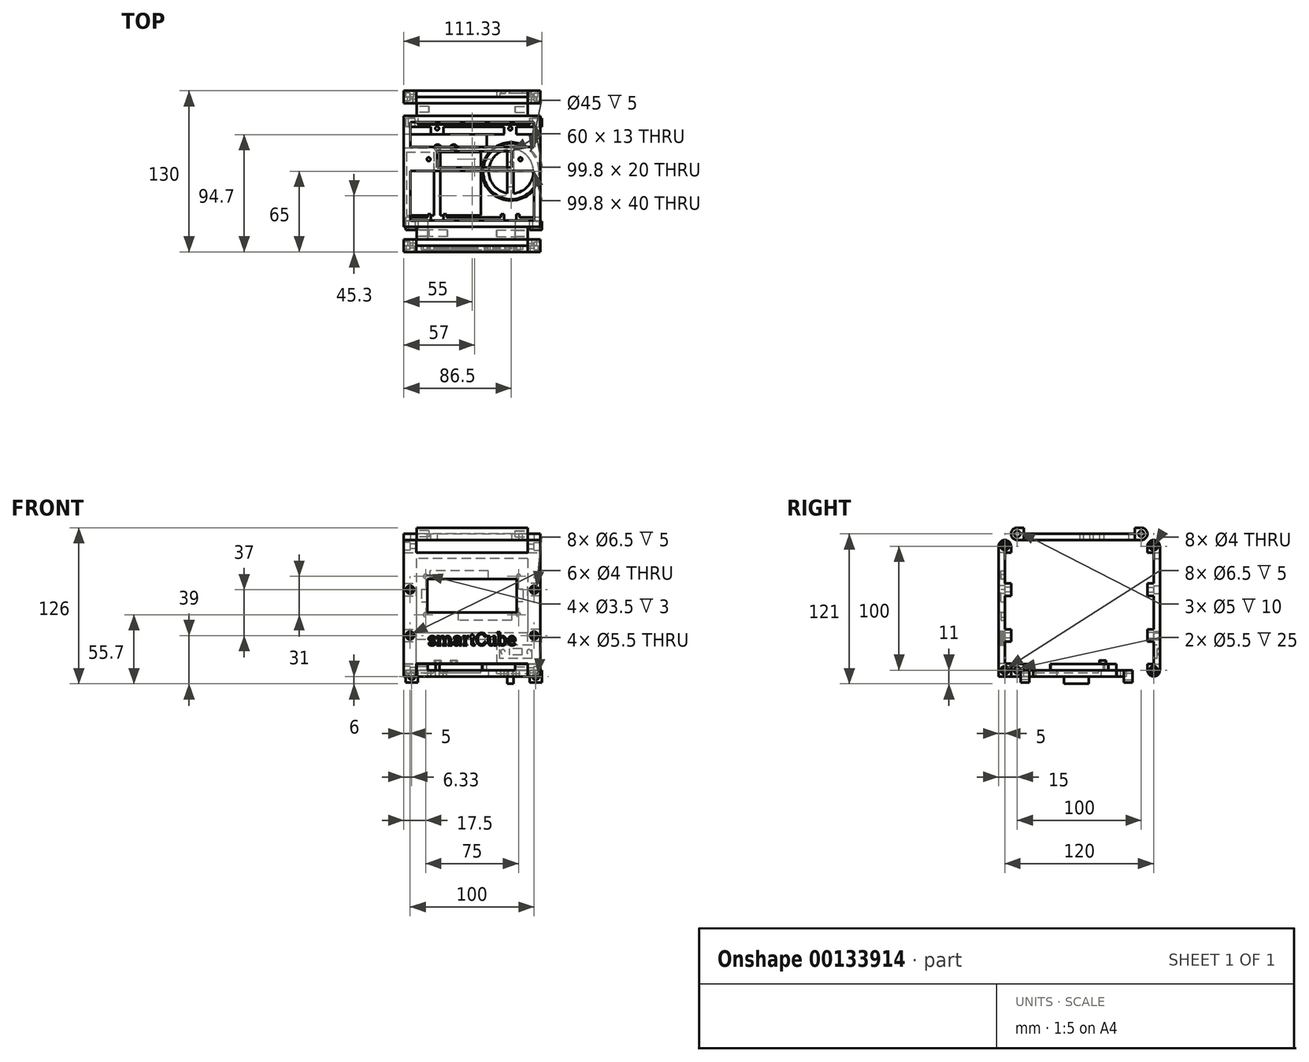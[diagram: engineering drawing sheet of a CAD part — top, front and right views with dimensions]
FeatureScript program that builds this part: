
annotation { "Feature Type Name" : "Feature", "Feature Type Description" : "" }
export const myFeature = defineFeature(function(context is Context, id is Id, definition is map)
    precondition{}
    {
        {
            assignVariable(context, id + "F0", {"name" : "wallthickness", "anyValue" : 10});
        }
        {
            var Q0;
            Q0=qCreatedBy(makeId("Top.planeOp"),FACE);
            var sketch = newSketch(context, id + "F1", { "sketchPlane" : qUnion([Q0])});
            skLineSegment(sketch, "E0.bottom", {"start": v(55, 55) * mm, "end": v(-55, 55) * mm});
            skLineSegment(sketch, "E0.top", {"start": v(55, -55) * mm, "end": v(-55, -55) * mm});
            skLineSegment(sketch, "E0.left", {"start": v(55, 55) * mm, "end": v(55, -55) * mm});
            skLineSegment(sketch, "E0.right", {"start": v(-55, 55) * mm, "end": v(-55, -55) * mm});
            skPoint(sketch, "E0.middle", {"position": v(0, 0) * mm});
            skSolve(sketch);
        }
        {
            var Q0;
            Q0 = qSketchRegion(id + "F1", true);
            var Q1;
            Q1=makeQuery(id+"F1.imprint","IMPRINT",FACE,{"disambiguationData":[TD([[makeQuery(id+"F1.imprint","IMPRINT",EDGE,{"derivedFrom":sQuery(id+"F1.wireOp",EDGE,"Ik4GJv2W-OQxF-1Uup-oVkI-S9FSixUqUyaa.bottom")}),1.0]])]});
            var Q2;
            Q2=makeQuery(id+"F1.imprint","IMPRINT",FACE,{"disambiguationData":[TD([[makeQuery(id+"F1.imprint","IMPRINT",EDGE,{"derivedFrom":sQuery(id+"F1.wireOp",EDGE,"4651642c-b40e-41a3-8e81-cadb49717aff")}),-1.0]])]});
            var Q3;
            Q3=makeQuery(id+"F1.imprint","IMPRINT",FACE,{"disambiguationData":[TD([[makeQuery(id+"F1.imprint","IMPRINT",EDGE,{"derivedFrom":sQuery(id+"F1.wireOp",EDGE,"6e1fa858-a5c8-444f-bbba-da70f5c4369a")}),-1.0]])]});
            var Q4;
            Q4=makeQuery(id+"F1.imprint","IMPRINT",FACE,{"disambiguationData":[TD([[makeQuery(id+"F1.imprint","IMPRINT",EDGE,{"derivedFrom":sQuery(id+"F1.wireOp",EDGE,"c5d3db0a-0530-42fc-989c-932ff3de016f")}),-1.0]])]});
            var Q5;
            Q5=makeQuery(id+"F1.imprint","IMPRINT",FACE,{"disambiguationData":[TD([[makeQuery(id+"F1.imprint","IMPRINT",EDGE,{"derivedFrom":sQuery(id+"F1.wireOp",EDGE,"a261eff7-1251-44c3-8bcb-5ba957302f77")}),-1.0]])]});
            extrude(context, id + "F2", {"entities" : qUnion([Q0, Q1, Q2, Q3, Q4, Q5]), "depth" : (getVariable(context, 'wallthickness')) * mm});
        }
        {
            var Q0;
            Q0=makeQuery(id+"F2.opExtrude","CAP_FACE",FACE,{"disambiguationData":[OSD([sQuery(id+"F1.wireOp",EDGE,"E0.bottom"),sQuery(id+"F1.wireOp",EDGE,"E0.top"),sQuery(id+"F1.wireOp",EDGE,"E0.left"),sQuery(id+"F1.wireOp",EDGE,"E0.right")])],"isStart":false});
            var sketch = newSketch(context, id + "F3", { "sketchPlane" : qUnion([Q0])});
            skLineSegment(sketch, "E1.bottom", {"start": v(55, 55) * mm, "end": v(44.8, 55) * mm});
            skLineSegment(sketch, "E1.top", {"start": v(55, 44.8) * mm, "end": v(44.8, 44.8) * mm});
            skLineSegment(sketch, "E1.left", {"start": v(55, 55) * mm, "end": v(55, 44.8) * mm});
            skLineSegment(sketch, "E1.right", {"start": v(44.8, 55) * mm, "end": v(44.8, 44.8) * mm});
            skLineSegment(sketch, "E2.bottom", {"start": v(-55, 55) * mm, "end": v(-44.8, 55) * mm});
            skLineSegment(sketch, "E2.top", {"start": v(-55, 44.8) * mm, "end": v(-44.8, 44.8) * mm});
            skLineSegment(sketch, "E2.left", {"start": v(-55, 55) * mm, "end": v(-55, 44.8) * mm});
            skLineSegment(sketch, "E2.right", {"start": v(-44.8, 55) * mm, "end": v(-44.8, 44.8) * mm});
            skLineSegment(sketch, "E3.bottom", {"start": v(-55, -55) * mm, "end": v(-44.8, -55) * mm});
            skLineSegment(sketch, "E3.top", {"start": v(-55, -44.8) * mm, "end": v(-44.8, -44.8) * mm});
            skLineSegment(sketch, "E3.left", {"start": v(-55, -55) * mm, "end": v(-55, -44.8) * mm});
            skLineSegment(sketch, "E3.right", {"start": v(-44.8, -55) * mm, "end": v(-44.8, -44.8) * mm});
            skLineSegment(sketch, "E4.bottom", {"start": v(55, -55) * mm, "end": v(44.8, -55) * mm});
            skLineSegment(sketch, "E4.top", {"start": v(55, -44.8) * mm, "end": v(44.8, -44.8) * mm});
            skLineSegment(sketch, "E4.left", {"start": v(55, -55) * mm, "end": v(55, -44.8) * mm});
            skLineSegment(sketch, "E4.right", {"start": v(44.8, -55) * mm, "end": v(44.8, -44.8) * mm});
            skSolve(sketch);
        }
        {
            var Q0;
            Q0 = qSketchRegion(id + "F3", true);
            extrude(context, id + "F4", {"entities" : qUnion([Q0]), "operationType" : NewBodyOperationType.REMOVE, "oppositeDirection" : true, "depth" : (getVariable(context, 'wallthickness')) * mm});
        }
        {
            var Q0;
            Q0=makeQuery(id+"F4.boolean.opBoolean","COPY",FACE,{"derivedFrom":makeQuery(id+"F4.opExtrude","SWEPT_FACE",FACE,{"disambiguationData":[OSD([sQuery(id+"F3.wireOp",EDGE,"E3.right")])]})});
            var sketch = newSketch(context, id + "F5", { "sketchPlane" : qUnion([Q0])});
            skCircle(sketch, "E5", {"center": v(50, 5) * mm, "radius": 2.75 * mm});
            skSolve(sketch);
        }
        {
            var Q0;
            Q0 = qSketchRegion(id + "F5", true);
            extrude(context, id + "F6", {"entities" : qUnion([Q0]), "operationType" : NewBodyOperationType.REMOVE, "oppositeDirection" : true, "depth" : 25 * mm});
        }
        {
            var Q0;
            Q0=makeQuery(id+"F4.boolean.opBoolean","COPY",FACE,{"derivedFrom":makeQuery(id+"F4.opExtrude","SWEPT_FACE",FACE,{"disambiguationData":[OSD([sQuery(id+"F3.wireOp",EDGE,"E4.right")])]})});
            var sketch = newSketch(context, id + "F7", { "sketchPlane" : qUnion([Q0])});
            skCircle(sketch, "E6", {"center": v(-50, 5) * mm, "radius": 2.75 * mm});
            skSolve(sketch);
        }
        {
            var Q0;
            Q0 = qSketchRegion(id + "F7", true);
            extrude(context, id + "F8", {"entities" : qUnion([Q0]), "operationType" : NewBodyOperationType.REMOVE, "oppositeDirection" : true, "depth" : 25 * mm});
        }
        {
            var Q0;
            Q0=makeQuery(id+"F4.boolean.opBoolean","COPY",FACE,{"derivedFrom":makeQuery(id+"F4.opExtrude","SWEPT_FACE",FACE,{"disambiguationData":[OSD([sQuery(id+"F3.wireOp",EDGE,"E2.right")])]})});
            var sketch = newSketch(context, id + "F9", { "sketchPlane" : qUnion([Q0])});
            skCircle(sketch, "E7", {"center": v(-50, 5) * mm, "radius": 2.75 * mm});
            skSolve(sketch);
        }
        {
            var Q0;
            Q0 = qSketchRegion(id + "F9", true);
            extrude(context, id + "F10", {"entities" : qUnion([Q0]), "operationType" : NewBodyOperationType.REMOVE, "oppositeDirection" : true, "depth" : 25 * mm});
        }
        {
            var Q0;
            Q0=makeQuery(id+"F4.boolean.opBoolean","COPY",FACE,{"derivedFrom":makeQuery(id+"F4.opExtrude","SWEPT_FACE",FACE,{"disambiguationData":[OSD([sQuery(id+"F3.wireOp",EDGE,"E1.right")])]})});
            var sketch = newSketch(context, id + "F11", { "sketchPlane" : qUnion([Q0])});
            skCircle(sketch, "E8", {"center": v(50, 5) * mm, "radius": 2.75 * mm});
            skSolve(sketch);
        }
        {
            var Q0;
            Q0 = qSketchRegion(id + "F11", true);
            extrude(context, id + "F12", {"entities" : qUnion([Q0]), "operationType" : NewBodyOperationType.REMOVE, "oppositeDirection" : true, "depth" : 25 * mm});
        }
        {
            var Q0;
            Q0=makeQuery(id+"F2.opExtrude","SWEPT_FACE",FACE,{"disambiguationData":[OSD([sQuery(id+"F1.wireOp",EDGE,"E0.top")])]});
            var sketch = newSketch(context, id + "F13", { "sketchPlane" : qUnion([Q0])});
            skLineSegment(sketch, "E9.0", {"start": v(55, 0) * mm, "end": v(-55, 0) * mm});
            skLineSegment(sketch, "E10.bottom", {"start": v(-55, 0) * mm, "end": v(55, 0) * mm});
            skLineSegment(sketch, "E10.top", {"start": v(-55, 110) * mm, "end": v(55, 110) * mm});
            skLineSegment(sketch, "E10.left", {"start": v(-55, 0) * mm, "end": v(-55, 110) * mm});
            skLineSegment(sketch, "E10.right", {"start": v(55, 0) * mm, "end": v(55, 110) * mm});
            skSolve(sketch);
        }
        {
            var Q0;
            Q0=makeQuery(id+"F13.imprint","IMPRINT",FACE,{"disambiguationData":[TD([[makeQuery(id+"F13.imprint","IMPRINT",EDGE,{"derivedFrom":sQuery(id+"F13.wireOp",EDGE,"E10.top")}),-1.0]])]});
            var Q1;
            {var subQ1=sQuery(id+"F1.wireOp",EDGE,"E0.top");Q1=makeQuery(id+"F13.imprint","IMPRINT",FACE,{"disambiguationData":[TD([[makeQuery(id+"F13.imprint","IMPRINT",EDGE,{"derivedFrom":makeQuery(id+"FIyDD7IV5j6uFW4_2.opFillet","BLEND_EDGE",EDGE,{"blendedFrom":[makeQuery(id+"F2.opExtrude","CAP_EDGE",EDGE,{"disambiguationData":[OSD([subQ1])],"isStart":false}),makeQuery(id+"F2.opExtrude","SWEPT_FACE",FACE,{"disambiguationData":[OSD([subQ1])]})],"blendedInto":[makeQuery(id+"F2.opExtrude","SWEPT_FACE",FACE,{"disambiguationData":[OSD([subQ1])]})]})}),1.0]])]});}
            extrude(context, id + "F14", {"entities" : qUnion([Q0, Q1]), "depth" : (getVariable(context, 'wallthickness')) * mm});
        }
        {
            var Q0;
            Q0=makeQuery(id+"F14.opExtrude","CAP_FACE",FACE,{"disambiguationData":[OSD([sQuery(id+"F13.wireOp",EDGE,"E10.bottom"),sQuery(id+"F13.wireOp",EDGE,"E10.top"),sQuery(id+"F13.wireOp",EDGE,"E10.left"),sQuery(id+"F13.wireOp",EDGE,"E10.right")])],"isStart":false});
            var sketch = newSketch(context, id + "F15", { "sketchPlane" : qUnion([Q0])});
            skLineSegment(sketch, "E11.bottom", {"start": v(-55, 0) * mm, "end": v(-45, 0) * mm});
            skLineSegment(sketch, "E11.top", {"start": v(-55, 10.2) * mm, "end": v(-45, 10.2) * mm});
            skLineSegment(sketch, "E11.left", {"start": v(-55, 0) * mm, "end": v(-55, 10.2) * mm});
            skLineSegment(sketch, "E11.right", {"start": v(-45, 0) * mm, "end": v(-45, 10.2) * mm});
            skLineSegment(sketch, "E12.bottom", {"start": v(55, 0) * mm, "end": v(45, 0) * mm});
            skLineSegment(sketch, "E12.top", {"start": v(55, 10.2) * mm, "end": v(45, 10.2) * mm});
            skLineSegment(sketch, "E12.left", {"start": v(55, 0) * mm, "end": v(55, 10.2) * mm});
            skLineSegment(sketch, "E12.right", {"start": v(45, 0) * mm, "end": v(45, 10.2) * mm});
            skLineSegment(sketch, "E13.bottom", {"start": v(-45, 10.2) * mm, "end": v(45, 10.2) * mm});
            skLineSegment(sketch, "E13.top", {"start": v(-45, 0) * mm, "end": v(45, 0) * mm});
            skLineSegment(sketch, "E13.left", {"start": v(-45, 10.2) * mm, "end": v(-45, 0) * mm});
            skLineSegment(sketch, "E13.right", {"start": v(45, 10.2) * mm, "end": v(45, 0) * mm});
            skSolve(sketch);
        }
        {
            var Q0;
            Q0=makeQuery(id+"F15.imprint","IMPRINT",FACE,{"disambiguationData":[TD([[makeQuery(id+"F15.imprint","IMPRINT",EDGE,{"derivedFrom":sQuery(id+"F15.wireOp",EDGE,"E13.bottom")}),-1.0]])]});
            extrude(context, id + "F16", {"entities" : qUnion([Q0]), "operationType" : NewBodyOperationType.REMOVE, "oppositeDirection" : true, "depth" : (getVariable(context, 'wallthickness')) * mm});
        }
        {
            var Q0;
            {var subQ2=sQuery(id+"F15.wireOp",EDGE,"E11.top");Q0=makeQuery(id+"F15.imprint","IMPRINT",FACE,{"disambiguationData":[TD([[makeQuery(id+"F15.imprint","IMPRINT",EDGE,{"derivedFrom":subQ2}),1.0]])]});}
            var sketch = newSketch(context, id + "F17", { "sketchPlane" : qUnion([Q0])});
            skLineSegment(sketch, "E14.bottom", {"start": v(36, 51.7) * mm, "end": v(-36, 51.7) * mm});
            skLineSegment(sketch, "E14.top", {"start": v(36, 78.7) * mm, "end": v(-36, 78.7) * mm});
            skLineSegment(sketch, "E14.left", {"start": v(36, 51.7) * mm, "end": v(36, 78.7) * mm});
            skLineSegment(sketch, "E14.right", {"start": v(-36, 51.7) * mm, "end": v(-36, 78.7) * mm});
            skPoint(sketch, "E14.middle", {"position": v(0, 65.2) * mm});
            skSolve(sketch);
        }
        {
            var Q0;
            Q0 = qSketchRegion(id + "F17", true);
            extrude(context, id + "F18", {"entities" : qUnion([Q0]), "operationType" : NewBodyOperationType.REMOVE, "oppositeDirection" : true, "depth" : (getVariable(context, 'wallthickness')) * mm});
        }
        {
            var Q0;
            Q0=makeQuery(id+"F14.opExtrude","CAP_FACE",FACE,{"disambiguationData":[OSD([sQuery(id+"F13.wireOp",EDGE,"E10.bottom"),sQuery(id+"F13.wireOp",EDGE,"E10.top"),sQuery(id+"F13.wireOp",EDGE,"E10.left"),sQuery(id+"F13.wireOp",EDGE,"E10.right")])],"isStart":true});
            var sketch = newSketch(context, id + "F19", { "sketchPlane" : qUnion([Q0])});
            skLineSegment(sketch, "E15.bottom", {"start": v(41, 45.2) * mm, "end": v(-41, 45.2) * mm});
            skLineSegment(sketch, "E15.top", {"start": v(41, 85.2) * mm, "end": v(-41, 85.2) * mm});
            skLineSegment(sketch, "E15.left", {"start": v(41, 45.2) * mm, "end": v(41, 85.2) * mm});
            skLineSegment(sketch, "E15.right", {"start": v(-41, 45.2) * mm, "end": v(-41, 85.2) * mm});
            skPoint(sketch, "E15.middle", {"position": v(0, 65.2) * mm});
            skSolve(sketch);
        }
        {
            var Q0;
            Q0 = qSketchRegion(id + "F19", true);
            extrude(context, id + "F20", {"entities" : qUnion([Q0]), "operationType" : NewBodyOperationType.REMOVE, "oppositeDirection" : true, "depth" : 5 * mm});
        }
        {
            var Q0;
            Q0=makeQuery(id+"F14.opExtrude","CAP_FACE",FACE,{"disambiguationData":[OSD([sQuery(id+"F13.wireOp",EDGE,"E10.bottom"),sQuery(id+"F13.wireOp",EDGE,"E10.top"),sQuery(id+"F13.wireOp",EDGE,"E10.left"),sQuery(id+"F13.wireOp",EDGE,"E10.right")])],"isStart":false});
            var sketch = newSketch(context, id + "F21", { "sketchPlane" : qUnion([Q0])});
            skLineSegment(sketch, "E16.bottom", {"start": v(55, 110) * mm, "end": v(45, 110) * mm});
            skLineSegment(sketch, "E16.top", {"start": v(55, 100) * mm, "end": v(45, 100) * mm});
            skLineSegment(sketch, "E16.left", {"start": v(55, 110) * mm, "end": v(55, 100) * mm});
            skLineSegment(sketch, "E16.right", {"start": v(45, 110) * mm, "end": v(45, 100) * mm});
            skLineSegment(sketch, "E17.bottom", {"start": v(-55, 110) * mm, "end": v(-45, 110) * mm});
            skLineSegment(sketch, "E17.top", {"start": v(-55, 100) * mm, "end": v(-45, 100) * mm});
            skLineSegment(sketch, "E17.left", {"start": v(-55, 110) * mm, "end": v(-55, 100) * mm});
            skLineSegment(sketch, "E17.right", {"start": v(-45, 110) * mm, "end": v(-45, 100) * mm});
            skLineSegment(sketch, "E18.bottom", {"start": v(-45, 110) * mm, "end": v(45, 110) * mm});
            skLineSegment(sketch, "E18.top", {"start": v(-45, 100) * mm, "end": v(45, 100) * mm});
            skSolve(sketch);
        }
        {
            var Q0;
            Q0=makeQuery(id+"F21.imprint","IMPRINT",FACE,{"disambiguationData":[TD([[makeQuery(id+"F21.imprint","IMPRINT",EDGE,{"derivedFrom":sQuery(id+"F21.wireOp",EDGE,"E18.bottom")}),-1.0]])]});
            extrude(context, id + "F22", {"entities" : qUnion([Q0]), "operationType" : NewBodyOperationType.REMOVE, "oppositeDirection" : true, "depth" : 12 * mm});
        }
        {
            var Q0;
            Q0=makeQuery(id+"F14.opExtrude","SWEPT_FACE",FACE,{"disambiguationData":[OSD([sQuery(id+"F13.wireOp",EDGE,"E10.right")])]});
            var sketch = newSketch(context, id + "F23", { "sketchPlane" : qUnion([Q0])});
            skCircle(sketch, "E19", {"center": v(-60, 105) * mm, "radius": 2 * mm});
            skCircle(sketch, "E20", {"center": v(-60, 105) * mm, "radius": 3.25 * mm});
            skCircle(sketch, "E21", {"center": v(-60, 5) * mm, "radius": 3.25 * mm});
            skCircle(sketch, "E22", {"center": v(-60, 5) * mm, "radius": 2 * mm});
            skSolve(sketch);
        }
        {
            var Q0;
            Q0=makeQuery(id+"F23.imprint","IMPRINT",FACE,{"disambiguationData":[TD([[makeQuery(id+"F23.imprint","IMPRINT",EDGE,{"derivedFrom":sQuery(id+"F23.wireOp",EDGE,"E19")}),1.0]])]});
            var Q1;
            Q1=makeQuery(id+"F23.imprint","IMPRINT",FACE,{"disambiguationData":[TD([[makeQuery(id+"F23.imprint","IMPRINT",EDGE,{"derivedFrom":sQuery(id+"F23.wireOp",EDGE,"E22")}),1.0]])]});
            var Q2;
            Q2=sQuery(id+"F23.wireOp",EDGE,"E19");
            extrude(context, id + "F24", {"entities" : qUnion([Q0, Q1]), "operationType" : NewBodyOperationType.REMOVE, "surfaceEntities" : qUnion([Q2]), "oppositeDirection" : true, "depth" : 25 * mm});
        }
        {
            var Q0;
            Q0=makeQuery(id+"F23.imprint","IMPRINT",FACE,{"disambiguationData":[TD([[makeQuery(id+"F23.imprint","IMPRINT",EDGE,{"derivedFrom":sQuery(id+"F23.wireOp",EDGE,"E19")}),-1.0]])]});
            var Q1;
            Q1=makeQuery(id+"F23.imprint","IMPRINT",FACE,{"disambiguationData":[TD([[makeQuery(id+"F23.imprint","IMPRINT",EDGE,{"derivedFrom":sQuery(id+"F23.wireOp",EDGE,"E21")}),1.0]])]});
            extrude(context, id + "F25", {"entities" : qUnion([Q0, Q1]), "operationType" : NewBodyOperationType.REMOVE, "oppositeDirection" : true, "depth" : 5 * mm});
        }
        {
            var Q0;
            Q0=makeQuery(id+"F14.opExtrude","SWEPT_FACE",FACE,{"disambiguationData":[OSD([sQuery(id+"F13.wireOp",EDGE,"E10.left")])]});
            var sketch = newSketch(context, id + "F26", { "sketchPlane" : qUnion([Q0])});
            skCircle(sketch, "E23", {"center": v(60, 105) * mm, "radius": 3.25 * mm});
            skCircle(sketch, "E24", {"center": v(60, 105) * mm, "radius": 2 * mm});
            skCircle(sketch, "E25", {"center": v(60, 5) * mm, "radius": 3.25 * mm});
            skCircle(sketch, "E26", {"center": v(60, 5) * mm, "radius": 2 * mm});
            skSolve(sketch);
        }
        {
            var Q0;
            Q0=makeQuery(id+"F26.imprint","IMPRINT",FACE,{"disambiguationData":[TD([[makeQuery(id+"F26.imprint","IMPRINT",EDGE,{"derivedFrom":sQuery(id+"F26.wireOp",EDGE,"E23")}),1.0]])]});
            var Q1;
            Q1=makeQuery(id+"F26.imprint","IMPRINT",FACE,{"disambiguationData":[TD([[makeQuery(id+"F26.imprint","IMPRINT",EDGE,{"derivedFrom":sQuery(id+"F26.wireOp",EDGE,"E25")}),1.0]])]});
            extrude(context, id + "F27", {"entities" : qUnion([Q0, Q1]), "operationType" : NewBodyOperationType.REMOVE, "oppositeDirection" : true, "depth" : 5 * mm});
        }
        {
            var Q0;
            Q0=makeQuery(id+"F27.boolean.opBoolean","SPLIT",FACE,{"disambiguationData":[TD([makeQuery(id+"F27.opExtrude","SWEPT_FACE",FACE,{"disambiguationData":[OSD([sQuery(id+"F26.wireOp",EDGE,"E26")])]})])],"derivedFrom":makeQuery(id+"F14.opExtrude","SWEPT_FACE",FACE,{"disambiguationData":[OSD([sQuery(id+"F13.wireOp",EDGE,"E10.left")])]})});
            var Q1;
            Q1=makeQuery(id+"F27.boolean.opBoolean","SPLIT",FACE,{"disambiguationData":[TD([makeQuery(id+"F27.opExtrude","SWEPT_FACE",FACE,{"disambiguationData":[OSD([sQuery(id+"F26.wireOp",EDGE,"E24")])]})])],"derivedFrom":makeQuery(id+"F14.opExtrude","SWEPT_FACE",FACE,{"disambiguationData":[OSD([sQuery(id+"F13.wireOp",EDGE,"E10.left")])]})});
            extrude(context, id + "F28", {"entities" : qUnion([Q0, Q1]), "operationType" : NewBodyOperationType.REMOVE, "oppositeDirection" : true, "depth" : 25 * mm});
        }
        {
            var Q0;
            Q0=makeQuery(id+"F2.opExtrude","CAP_FACE",FACE,{"disambiguationData":[OSD([sQuery(id+"F1.wireOp",EDGE,"E0.bottom"),sQuery(id+"F1.wireOp",EDGE,"E0.top"),sQuery(id+"F1.wireOp",EDGE,"E0.left"),sQuery(id+"F1.wireOp",EDGE,"E0.right"),sQuery(id+"F1.wireOp",EDGE,"d97dc57c-63e8-403d-9b24-ca8aebbb670c.bottom"),sQuery(id+"F1.wireOp",EDGE,"d97dc57c-63e8-403d-9b24-ca8aebbb670c.top"),sQuery(id+"F1.wireOp",EDGE,"d97dc57c-63e8-403d-9b24-ca8aebbb670c.left"),sQuery(id+"F1.wireOp",EDGE,"d97dc57c-63e8-403d-9b24-ca8aebbb670c.right"),sQuery(id+"F1.wireOp",EDGE,"989d19cf-17dd-4a0b-bbe1-a7268cc939a1")])],"isStart":false});
            var sketch = newSketch(context, id + "F29", { "sketchPlane" : qUnion([Q0])});
            skLineSegment(sketch, "E27.bottom", {"start": v(-12.8, 50) * mm, "end": v(-29.8, 50) * mm, "construction": true});
            skLineSegment(sketch, "E27.left", {"start": v(-12.8, 50) * mm, "end": v(-12.8, 19) * mm, "construction": true});
            skLineSegment(sketch, "E27.right", {"start": v(-29.8, 50) * mm, "end": v(-29.8, 19) * mm, "construction": true});
            skLineSegment(sketch, "E28.bottom", {"start": v(-29.8, 50) * mm, "end": v(-27.8, 50) * mm, "construction": true});
            skLineSegment(sketch, "E28.left", {"start": v(-29.8, 50) * mm, "end": v(-29.8, 48) * mm, "construction": true});
            skLineSegment(sketch, "E29.bottom", {"start": v(-12.8, 50) * mm, "end": v(-14.8, 50) * mm, "construction": true});
            skLineSegment(sketch, "E29.left", {"start": v(-12.8, 50) * mm, "end": v(-12.8, 48) * mm, "construction": true});
            skLineSegment(sketch, "E30.left", {"start": v(-29.8, 19) * mm, "end": v(-29.8, 21) * mm, "construction": true});
            skLineSegment(sketch, "E31.left", {"start": v(-12.8, 19) * mm, "end": v(-12.8, 21) * mm, "construction": true});
            skCircle(sketch, "E32", {"center": v(-29.8, 50) * mm, "radius": 1.5 * mm});
            skCircle(sketch, "E33", {"center": v(-29.8, 50) * mm, "radius": 2.75 * mm});
            skCircle(sketch, "E34", {"center": v(-12.8, 50) * mm, "radius": 1.47 * mm});
            skCircle(sketch, "E35", {"center": v(-12.8, 50) * mm, "radius": 2.75 * mm});
            skCircle(sketch, "E36", {"center": v(-14.8, 19) * mm, "radius": 2.75 * mm});
            skCircle(sketch, "E37", {"center": v(-27.8, 19) * mm, "radius": 1.5 * mm});
            skCircle(sketch, "E38", {"center": v(-27.8, 19) * mm, "radius": 2.75 * mm});
            skCircle(sketch, "E39", {"center": v(-14.8, 19) * mm, "radius": 1.47 * mm});
            skLineSegment(sketch, "E40", {"start": v(-12.8, 19) * mm, "end": v(-14.8, 19) * mm, "construction": true});
            skLineSegment(sketch, "E41", {"start": v(-29.8, 19) * mm, "end": v(-27.8, 19) * mm, "construction": true});
            skSolve(sketch);
        }
        {
            var Q0;
            Q0 = qSketchRegion(id + "F29", true);
            extrude(context, id + "F30", {"entities" : qUnion([Q0]), "operationType" : NewBodyOperationType.ADD, "depth" : 3 * mm});
        }
        {
            var Q0;
            Q0=makeQuery(id+"F29.imprint","IMPRINT",FACE,{"disambiguationData":[TD([[makeQuery(id+"F29.imprint","IMPRINT",EDGE,{"derivedFrom":sQuery(id+"F29.wireOp",EDGE,"E32")}),1.0]])]});
            var Q1;
            Q1=makeQuery(id+"F29.imprint","IMPRINT",FACE,{"disambiguationData":[TD([[makeQuery(id+"F29.imprint","IMPRINT",EDGE,{"derivedFrom":sQuery(id+"F29.wireOp",EDGE,"E34")}),1.0]])]});
            var Q2;
            Q2=makeQuery(id+"F29.imprint","IMPRINT",FACE,{"disambiguationData":[TD([[makeQuery(id+"F29.imprint","IMPRINT",EDGE,{"derivedFrom":sQuery(id+"F29.wireOp",EDGE,"08cefe6c-77fe-49f1-80db-ca5d153754f9")}),1.0]])]});
            var Q3;
            Q3=makeQuery(id+"F29.imprint","IMPRINT",FACE,{"disambiguationData":[TD([[makeQuery(id+"F29.imprint","IMPRINT",EDGE,{"derivedFrom":sQuery(id+"F29.wireOp",EDGE,"E37")}),1.0]])]});
            extrude(context, id + "F31", {"entities" : qUnion([Q0, Q1, Q2, Q3]), "operationType" : NewBodyOperationType.REMOVE, "oppositeDirection" : true, "depth" : 6 * mm});
        }
        {
            var Q0;
            Q0=makeQuery(id+"F2.opExtrude","SWEPT_FACE",FACE,{"disambiguationData":[OSD([sQuery(id+"F1.wireOp",EDGE,"E0.bottom")])]});
            var sketch = newSketch(context, id + "F32", { "sketchPlane" : qUnion([Q0])});
            skPoint(sketch, "E42.0", {"position": v(-44.8, 0) * mm});
            skLineSegment(sketch, "E43.0", {"start": v(-55, 0) * mm, "end": v(55, 0) * mm});
            skLineSegment(sketch, "E44.top", {"start": v(-55, 110) * mm, "end": v(55, 110) * mm});
            skLineSegment(sketch, "E44.left", {"start": v(-55, 0) * mm, "end": v(-55, 110) * mm});
            skLineSegment(sketch, "E44.right", {"start": v(55, 0) * mm, "end": v(55, 110) * mm});
            skSolve(sketch);
        }
        {
            var Q0;
            Q0 = qSketchRegion(id + "F32", true);
            extrude(context, id + "F33", {"entities" : qUnion([Q0]), "depth" : getVariable(context, 'wallthickness') * mm});
        }
        {
            var Q0;
            Q0=makeQuery(id+"F33.opExtrude","CAP_FACE",FACE,{"disambiguationData":[OSD([sQuery(id+"F32.wireOp",EDGE,"E43.0"),sQuery(id+"F32.wireOp",EDGE,"E44.top"),sQuery(id+"F32.wireOp",EDGE,"E44.left"),sQuery(id+"F32.wireOp",EDGE,"E44.right")])],"isStart":false});
            var sketch = newSketch(context, id + "F34", { "sketchPlane" : qUnion([Q0])});
            skLineSegment(sketch, "E45.bottom", {"start": v(-55, 0) * mm, "end": v(-45, 0) * mm});
            skLineSegment(sketch, "E45.top", {"start": v(-55, 10) * mm, "end": v(-45, 10) * mm});
            skLineSegment(sketch, "E45.left", {"start": v(-55, 0) * mm, "end": v(-55, 10) * mm});
            skLineSegment(sketch, "E45.right", {"start": v(-45, 0) * mm, "end": v(-45, 10) * mm});
            skLineSegment(sketch, "E46.bottom", {"start": v(55, 0) * mm, "end": v(45, 0) * mm});
            skLineSegment(sketch, "E46.top", {"start": v(55, 10) * mm, "end": v(45, 10) * mm});
            skLineSegment(sketch, "E46.left", {"start": v(55, 0) * mm, "end": v(55, 10) * mm});
            skLineSegment(sketch, "E46.right", {"start": v(45, 0) * mm, "end": v(45, 10) * mm});
            skPoint(sketch, "E47.0", {"position": v(12.8, 10) * mm});
            skLineSegment(sketch, "E48.0.1", {"start": v(-55, 0) * mm, "end": v(55, 0) * mm});
            skLineSegment(sketch, "E48.0.3", {"start": v(55, 0) * mm, "end": v(-55, 0) * mm});
            skLineSegment(sketch, "E49.bottom", {"start": v(45, 0) * mm, "end": v(34.8, 0) * mm});
            skLineSegment(sketch, "E50.bottom", {"start": v(-45, 10) * mm, "end": v(45, 10) * mm});
            skLineSegment(sketch, "E50.top", {"start": v(-45, 0) * mm, "end": v(45, 0) * mm});
            skLineSegment(sketch, "E50.left", {"start": v(-45, 10) * mm, "end": v(-45, 0) * mm});
            skLineSegment(sketch, "E50.right", {"start": v(45, 10) * mm, "end": v(45, 0) * mm});
            skLineSegment(sketch, "E51.top", {"start": v(34.8, 0) * mm, "end": v(45, 0) * mm});
            skLineSegment(sketch, "E52.bottom", {"start": v(40.72, 0) * mm, "end": v(45, 0) * mm});
            skLineSegment(sketch, "E53.bottom", {"start": v(-55, 110) * mm, "end": v(-45, 110) * mm, "construction": true});
            skLineSegment(sketch, "E53.top", {"start": v(-55, 100) * mm, "end": v(-45, 100) * mm, "construction": true});
            skLineSegment(sketch, "E53.left", {"start": v(-55, 110) * mm, "end": v(-55, 100) * mm, "construction": true});
            skLineSegment(sketch, "E53.right", {"start": v(-45, 110) * mm, "end": v(-45, 100) * mm});
            skLineSegment(sketch, "E54.bottom", {"start": v(55, 110) * mm, "end": v(45, 110) * mm, "construction": true});
            skLineSegment(sketch, "E54.top", {"start": v(55, 100) * mm, "end": v(45, 100) * mm, "construction": true});
            skLineSegment(sketch, "E54.left", {"start": v(55, 110) * mm, "end": v(55, 100) * mm, "construction": true});
            skLineSegment(sketch, "E54.right", {"start": v(45, 110) * mm, "end": v(45, 100) * mm, "construction": true});
            skLineSegment(sketch, "E55.bottom", {"start": v(-45, 110) * mm, "end": v(45, 110) * mm});
            skLineSegment(sketch, "E55.top", {"start": v(-45, 100) * mm, "end": v(45, 100) * mm});
            skLineSegment(sketch, "E55.right", {"start": v(45, 110) * mm, "end": v(45, 100) * mm});
            skLineSegment(sketch, "E56.bottom", {"start": v(45, 0) * mm, "end": v(-7, 0) * mm});
            skSolve(sketch);
        }
        {
            var Q0;
            Q0=makeQuery(id+"F34.imprint","IMPRINT",FACE,{"disambiguationData":[TD([[makeQuery(id+"F34.imprint","IMPRINT",EDGE,{"derivedFrom":sQuery(id+"F34.wireOp",EDGE,"E50.bottom")}),-1.0]])]});
            var Q1;
            {var subQ3=sQuery(id+"F34.wireOp",EDGE,"E52.bottom");Q1=makeQuery(id+"F34.imprint","IMPRINT",FACE,{"disambiguationData":[TD([[makeQuery(id+"F34.imprint","IMPRINT",EDGE,{"derivedFrom":subQ3}),1.0]])]});}
            var Q2;
            Q2=makeQuery(id+"F34.imprint","IMPRINT",FACE,{"disambiguationData":[TD([[makeQuery(id+"F34.imprint","IMPRINT",EDGE,{"derivedFrom":sQuery(id+"F34.wireOp",EDGE,"E55.bottom")}),-1.0]])]});
            var Q3;
            Q3=makeQuery(id+"F34.imprint","IMPRINT",FACE,{"disambiguationData":[TD([[makeQuery(id+"F34.imprint","IMPRINT",EDGE,{"derivedFrom":sQuery(id+"F34.wireOp",EDGE,"837d87b9-64d4-4556-9653-1f457b766715.bottom")}),-1.0]])]});
            var Q4;
            Q4=makeQuery(id+"F33.opExtrude","CAP_FACE",FACE,{"disambiguationData":[OSD([sQuery(id+"F32.wireOp",EDGE,"E43.0"),sQuery(id+"F32.wireOp",EDGE,"E44.top"),sQuery(id+"F32.wireOp",EDGE,"E44.left"),sQuery(id+"F32.wireOp",EDGE,"E44.right")])],"isStart":true});
            extrude(context, id + "F35", {"entities" : qUnion([Q0, Q1, Q2, Q3, Q4]), "operationType" : NewBodyOperationType.REMOVE, "oppositeDirection" : true, "depth" : 25 * mm});
        }
        {
            var Q0;
            Q0=makeQuery(id+"F33.opExtrude","SWEPT_FACE",FACE,{"disambiguationData":[OSD([sQuery(id+"F32.wireOp",EDGE,"E44.right")])]});
            var sketch = newSketch(context, id + "F36", { "sketchPlane" : qUnion([Q0])});
            skCircle(sketch, "E57", {"center": v(-60, 5) * mm, "radius": 2 * mm});
            skCircle(sketch, "E58", {"center": v(-60, 5) * mm, "radius": 3.25 * mm});
            skCircle(sketch, "E59", {"center": v(-60, 105) * mm, "radius": 2 * mm});
            skCircle(sketch, "E60", {"center": v(-60, 105) * mm, "radius": 3.25 * mm});
            skSolve(sketch);
        }
        {
            var Q0;
            Q0=makeQuery(id+"F36.imprint","IMPRINT",FACE,{"disambiguationData":[TD([[makeQuery(id+"F36.imprint","IMPRINT",EDGE,{"derivedFrom":sQuery(id+"F36.wireOp",EDGE,"E57")}),1.0]])]});
            var Q1;
            Q1=makeQuery(id+"F36.imprint","IMPRINT",FACE,{"disambiguationData":[TD([[makeQuery(id+"F36.imprint","IMPRINT",EDGE,{"derivedFrom":sQuery(id+"F36.wireOp",EDGE,"E59")}),1.0]])]});
            extrude(context, id + "F37", {"entities" : qUnion([Q0, Q1]), "operationType" : NewBodyOperationType.REMOVE, "oppositeDirection" : true, "depth" : getVariable(context, 'wallthickness') * mm});
        }
        {
            var Q0;
            Q0 = qSketchRegion(id + "F36", true);
            extrude(context, id + "F38", {"entities" : qUnion([Q0]), "operationType" : NewBodyOperationType.REMOVE, "oppositeDirection" : true, "depth" : 5 * mm});
        }
        {
            var Q0;
            Q0=makeQuery(id+"F33.opExtrude","SWEPT_FACE",FACE,{"disambiguationData":[OSD([sQuery(id+"F32.wireOp",EDGE,"E44.left")])]});
            var sketch = newSketch(context, id + "F39", { "sketchPlane" : qUnion([Q0])});
            skCircle(sketch, "E61", {"center": v(60, 5) * mm, "radius": 2 * mm});
            skCircle(sketch, "E62", {"center": v(60, 5) * mm, "radius": 3.25 * mm});
            skCircle(sketch, "E63", {"center": v(60, 105) * mm, "radius": 2 * mm});
            skCircle(sketch, "E64", {"center": v(60, 105) * mm, "radius": 3.25 * mm});
            skSolve(sketch);
        }
        {
            var Q0;
            Q0=makeQuery(id+"F39.imprint","IMPRINT",FACE,{"disambiguationData":[TD([[makeQuery(id+"F39.imprint","IMPRINT",EDGE,{"derivedFrom":sQuery(id+"F39.wireOp",EDGE,"E61")}),1.0]])]});
            var Q1;
            Q1=makeQuery(id+"F39.imprint","IMPRINT",FACE,{"disambiguationData":[TD([[makeQuery(id+"F39.imprint","IMPRINT",EDGE,{"derivedFrom":sQuery(id+"F39.wireOp",EDGE,"E63")}),1.0]])]});
            extrude(context, id + "F40", {"entities" : qUnion([Q0, Q1]), "operationType" : NewBodyOperationType.REMOVE, "oppositeDirection" : true, "depth" : 10 * mm});
        }
        {
            var Q0;
            Q0 = qSketchRegion(id + "F39", true);
            extrude(context, id + "F41", {"entities" : qUnion([Q0]), "operationType" : NewBodyOperationType.REMOVE, "oppositeDirection" : true, "depth" : 5 * mm});
        }
        {
            var Q0;
            {var subQ1=sQuery(id+"F13.wireOp",EDGE,"E10.left");var subQ2=sQuery(id+"F13.wireOp",EDGE,"E10.top");Q0=makeQuery(id+"F22.boolean.opBoolean","SPLIT",FACE,{"disambiguationData":[TD([makeQuery(id+"F14.opExtrude","SWEPT_FACE",FACE,{"disambiguationData":[OSD([subQ1])]})])],"derivedFrom":makeQuery(id+"F14.opExtrude","SWEPT_FACE",FACE,{"disambiguationData":[OSD([subQ2])]})});}
            var sketch = newSketch(context, id + "F42", { "sketchPlane" : qUnion([Q0])});
            skLineSegment(sketch, "E65.bottom", {"start": v(-55, -55) * mm, "end": v(55, -55) * mm});
            skLineSegment(sketch, "E65.top", {"start": v(-55, 55) * mm, "end": v(55, 55) * mm});
            skLineSegment(sketch, "E65.left", {"start": v(-55, -55) * mm, "end": v(-55, 55) * mm});
            skLineSegment(sketch, "E65.right", {"start": v(55, -55) * mm, "end": v(55, 55) * mm});
            skSolve(sketch);
        }
        {
            var Q0;
            Q0 = qSketchRegion(id + "F42", true);
            extrude(context, id + "F43", {"entities" : qUnion([Q0]), "depth" : getVariable(context, 'wallthickness') * mm});
        }
        {
            var Q0;
            Q0=makeQuery(id+"F43.opExtrude","CAP_FACE",FACE,{"disambiguationData":[OSD([sQuery(id+"F42.wireOp",EDGE,"E65.bottom"),sQuery(id+"F42.wireOp",EDGE,"E65.top"),sQuery(id+"F42.wireOp",EDGE,"E65.left"),sQuery(id+"F42.wireOp",EDGE,"E65.right")])],"isStart":false});
            var sketch = newSketch(context, id + "F44", { "sketchPlane" : qUnion([Q0])});
            skLineSegment(sketch, "E66.bottom", {"start": v(-55, 55) * mm, "end": v(-44.8, 55) * mm});
            skLineSegment(sketch, "E66.top", {"start": v(-55, 44.8) * mm, "end": v(-44.8, 44.8) * mm});
            skLineSegment(sketch, "E66.left", {"start": v(-55, 55) * mm, "end": v(-55, 44.8) * mm});
            skLineSegment(sketch, "E66.right", {"start": v(-44.8, 55) * mm, "end": v(-44.8, 44.8) * mm});
            skLineSegment(sketch, "E67.bottom", {"start": v(55, 55) * mm, "end": v(44.8, 55) * mm});
            skLineSegment(sketch, "E67.top", {"start": v(55, 44.8) * mm, "end": v(44.8, 44.8) * mm});
            skLineSegment(sketch, "E67.left", {"start": v(55, 55) * mm, "end": v(55, 44.8) * mm});
            skLineSegment(sketch, "E67.right", {"start": v(44.8, 55) * mm, "end": v(44.8, 44.8) * mm});
            skLineSegment(sketch, "E68.bottom", {"start": v(-55, -55) * mm, "end": v(-44.8, -55) * mm});
            skLineSegment(sketch, "E68.top", {"start": v(-55, -44.8) * mm, "end": v(-44.8, -44.8) * mm});
            skLineSegment(sketch, "E68.left", {"start": v(-55, -55) * mm, "end": v(-55, -44.8) * mm});
            skLineSegment(sketch, "E68.right", {"start": v(-44.8, -55) * mm, "end": v(-44.8, -44.8) * mm});
            skLineSegment(sketch, "E69.bottom", {"start": v(55, -55) * mm, "end": v(44.8, -55) * mm});
            skLineSegment(sketch, "E69.top", {"start": v(55, -44.8) * mm, "end": v(44.8, -44.8) * mm});
            skLineSegment(sketch, "E69.left", {"start": v(55, -55) * mm, "end": v(55, -44.8) * mm});
            skLineSegment(sketch, "E69.right", {"start": v(44.8, -55) * mm, "end": v(44.8, -44.8) * mm});
            skSolve(sketch);
        }
        {
            var Q0;
            Q0 = qSketchRegion(id + "F44", true);
            extrude(context, id + "F45", {"entities" : qUnion([Q0]), "operationType" : NewBodyOperationType.REMOVE, "oppositeDirection" : true, "depth" : getVariable(context, 'wallthickness') * mm});
        }
        {
            var Q0;
            Q0=makeQuery(id+"F45.boolean.opBoolean","COPY",FACE,{"derivedFrom":makeQuery(id+"F45.opExtrude","SWEPT_FACE",FACE,{"disambiguationData":[OSD([sQuery(id+"F44.wireOp",EDGE,"E69.right")])]})});
            var sketch = newSketch(context, id + "F46", { "sketchPlane" : qUnion([Q0])});
            skCircle(sketch, "E70", {"center": v(-50, 115) * mm, "radius": 2.5 * mm});
            skCircle(sketch, "E71", {"center": v(50, 115) * mm, "radius": 2.36 * mm});
            skSolve(sketch);
        }
        {
            var Q0;
            Q0=makeQuery(id+"F46.imprint","IMPRINT",FACE,{"disambiguationData":[TD([[makeQuery(id+"F46.imprint","IMPRINT",EDGE,{"derivedFrom":sQuery(id+"F46.wireOp",EDGE,"E71")}),1.0]])]});
            var Q1;
            Q1=makeQuery(id+"F46.imprint","IMPRINT",FACE,{"disambiguationData":[TD([[makeQuery(id+"F46.imprint","IMPRINT",EDGE,{"derivedFrom":sQuery(id+"F46.wireOp",EDGE,"E70")}),1.0]])]});
            extrude(context, id + "F47", {"entities" : qUnion([Q0, Q1]), "operationType" : NewBodyOperationType.REMOVE, "oppositeDirection" : true, "depth" : 10 * mm});
        }
        {
            var Q0;
            Q0=makeQuery(id+"F45.boolean.opBoolean","COPY",FACE,{"derivedFrom":makeQuery(id+"F45.opExtrude","SWEPT_FACE",FACE,{"disambiguationData":[OSD([sQuery(id+"F44.wireOp",EDGE,"E66.right")])]})});
            var sketch = newSketch(context, id + "F48", { "sketchPlane" : qUnion([Q0])});
            skCircle(sketch, "E72", {"center": v(-50, 115) * mm, "radius": 2.5 * mm});
            skCircle(sketch, "E73", {"center": v(50, 115) * mm, "radius": 2.5 * mm});
            skSolve(sketch);
        }
        {
            var Q0;
            Q0 = qSketchRegion(id + "F48", true);
            extrude(context, id + "F49", {"entities" : qUnion([Q0]), "operationType" : NewBodyOperationType.REMOVE, "oppositeDirection" : true, "depth" : 10 * mm});
        }
        {
            var Q0;
            Q0=makeQuery(id+"F33.opExtrude","CAP_FACE",FACE,{"disambiguationData":[OSD([sQuery(id+"F32.wireOp",EDGE,"E43.0"),sQuery(id+"F32.wireOp",EDGE,"E44.top"),sQuery(id+"F32.wireOp",EDGE,"E44.left"),sQuery(id+"F32.wireOp",EDGE,"E44.right")])],"isStart":true});
            var sketch = newSketch(context, id + "F50", { "sketchPlane" : qUnion([Q0])});
            skLineSegment(sketch, "E74.bottom", {"start": v(-55, 100) * mm, "end": v(55, 100) * mm});
            skLineSegment(sketch, "E74.top", {"start": v(-55, 10) * mm, "end": v(55, 10) * mm});
            skLineSegment(sketch, "E74.left", {"start": v(-55, 100) * mm, "end": v(-55, 10) * mm});
            skLineSegment(sketch, "E74.right", {"start": v(55, 100) * mm, "end": v(55, 10) * mm});
            skSolve(sketch);
        }
        {
            var Q0;
            Q0 = qSketchRegion(id + "F50", true);
            extrude(context, id + "F51", {"entities" : qUnion([Q0]), "operationType" : NewBodyOperationType.REMOVE, "oppositeDirection" : true, "depth" : 5 * mm});
        }
        {
            var Q0;
            Q0=makeQuery(id+"F20.boolean.opBoolean","COPY",FACE,{"derivedFrom":makeQuery(id+"F20.opExtrude","CAP_FACE",FACE,{"disambiguationData":[OSD([sQuery(id+"F19.wireOp",EDGE,"E15.bottom"),sQuery(id+"F19.wireOp",EDGE,"E15.top"),sQuery(id+"F19.wireOp",EDGE,"E15.left"),sQuery(id+"F19.wireOp",EDGE,"E15.right")])],"isStart":false})});
            var sketch = newSketch(context, id + "F52", { "sketchPlane" : qUnion([Q0])});
            skLineSegment(sketch, "E75.bottom", {"start": v(41, 70.2) * mm, "end": v(36, 70.2) * mm});
            skLineSegment(sketch, "E75.top", {"start": v(41, 60.2) * mm, "end": v(36, 60.2) * mm});
            skLineSegment(sketch, "E75.left", {"start": v(41, 70.2) * mm, "end": v(41, 60.2) * mm});
            skLineSegment(sketch, "E75.right", {"start": v(36, 70.2) * mm, "end": v(36, 60.2) * mm});
            skLineSegment(sketch, "E76.bottom", {"start": v(-31.79, 51.7) * mm, "end": v(11.21, 51.7) * mm});
            skLineSegment(sketch, "E76.top", {"start": v(-31.79, 45.2) * mm, "end": v(11.21, 45.2) * mm});
            skLineSegment(sketch, "E76.left", {"start": v(-31.79, 51.7) * mm, "end": v(-31.79, 45.2) * mm});
            skLineSegment(sketch, "E76.right", {"start": v(11.21, 51.7) * mm, "end": v(11.21, 45.2) * mm});
            skLineSegment(sketch, "E77", {"start": v(0, 78.7) * mm, "end": v(0, 51.7) * mm, "construction": true});
            skLineSegment(sketch, "E78", {"start": v(36, 65.2) * mm, "end": v(-36, 65.2) * mm, "construction": true});
            skLineSegment(sketch, "E79.bottom", {"start": v(-37.5, 49.7) * mm, "end": v(37.5, 49.7) * mm, "construction": true});
            skLineSegment(sketch, "E79.top", {"start": v(-37.5, 80.7) * mm, "end": v(37.5, 80.7) * mm, "construction": true});
            skLineSegment(sketch, "E79.left", {"start": v(-37.5, 49.7) * mm, "end": v(-37.5, 80.7) * mm, "construction": true});
            skLineSegment(sketch, "E79.right", {"start": v(37.5, 49.7) * mm, "end": v(37.5, 80.7) * mm, "construction": true});
            skPoint(sketch, "E79.middle", {"position": v(0, 65.2) * mm});
            skCircle(sketch, "E80", {"center": v(-37.5, 80.7) * mm, "radius": 1.75 * mm});
            skCircle(sketch, "E81", {"center": v(37.5, 80.7) * mm, "radius": 1.75 * mm});
            skCircle(sketch, "E82", {"center": v(37.5, 49.7) * mm, "radius": 1.75 * mm});
            skCircle(sketch, "E83", {"center": v(-37.5, 49.7) * mm, "radius": 1.75 * mm});
            skLineSegment(sketch, "E84.bottom", {"start": v(34, 78.7) * mm, "end": v(-13, 78.7) * mm});
            skLineSegment(sketch, "E84.top", {"start": v(34, 85.2) * mm, "end": v(-13, 85.2) * mm});
            skLineSegment(sketch, "E84.left", {"start": v(34, 78.7) * mm, "end": v(34, 85.2) * mm});
            skLineSegment(sketch, "E84.right", {"start": v(-13, 78.7) * mm, "end": v(-13, 85.2) * mm});
            skLineSegment(sketch, "E85.bottom", {"start": v(-41, 60.2) * mm, "end": v(-36, 60.2) * mm});
            skLineSegment(sketch, "E85.top", {"start": v(-41, 70.2) * mm, "end": v(-36, 70.2) * mm});
            skLineSegment(sketch, "E85.left", {"start": v(-41, 60.2) * mm, "end": v(-41, 70.2) * mm});
            skLineSegment(sketch, "E85.right", {"start": v(-36, 60.2) * mm, "end": v(-36, 70.2) * mm});
            skSolve(sketch);
        }
        {
            var Q0;
            Q0 = qSketchRegion(id + "F52", true);
            extrude(context, id + "F53", {"entities" : qUnion([Q0]), "operationType" : NewBodyOperationType.REMOVE, "oppositeDirection" : true, "depth" : 3 * mm});
        }
        {
            var Q0;
            Q0=makeQuery(id+"F14.opExtrude","CAP_FACE",FACE,{"disambiguationData":[OSD([sQuery(id+"F1.wireOp",EDGE,"E0.top"),sQuery(id+"F3.wireOp",EDGE,"E3.bottom"),sQuery(id+"F3.wireOp",EDGE,"E3.right"),sQuery(id+"F3.wireOp",EDGE,"E4.bottom"),sQuery(id+"F3.wireOp",EDGE,"E4.right"),sQuery(id+"F13.wireOp",EDGE,"E10.bottom"),sQuery(id+"F13.wireOp",EDGE,"E10.top"),sQuery(id+"F13.wireOp",EDGE,"E10.left"),sQuery(id+"F13.wireOp",EDGE,"E10.right")])],"isStart":true});
            var sketch = newSketch(context, id + "F54", { "sketchPlane" : qUnion([Q0])});
            skLineSegment(sketch, "E86.bottom", {"start": v(-45, 10.2) * mm, "end": v(45, 10.2) * mm});
            skLineSegment(sketch, "E86.top", {"start": v(-45, 100) * mm, "end": v(45, 100) * mm});
            skLineSegment(sketch, "E86.left", {"start": v(-45, 10.2) * mm, "end": v(-45, 100) * mm});
            skLineSegment(sketch, "E86.right", {"start": v(45, 10.2) * mm, "end": v(45, 100) * mm});
            skPoint(sketch, "E87.oppositeSnap0", {"position": v(55, 55) * mm});
            skLineSegment(sketch, "E87.bottom", {"start": v(45, 100) * mm, "end": v(55, 100) * mm});
            skLineSegment(sketch, "E87.top", {"start": v(45, 10.2) * mm, "end": v(55, 10.2) * mm});
            skLineSegment(sketch, "E87.left", {"start": v(45, 100) * mm, "end": v(45, 10.2) * mm});
            skLineSegment(sketch, "E87.right", {"start": v(55, 100) * mm, "end": v(55, 10.2) * mm});
            skLineSegment(sketch, "E88.bottom", {"start": v(-45, 100) * mm, "end": v(-55, 100) * mm});
            skLineSegment(sketch, "E88.top", {"start": v(-45, 10.2) * mm, "end": v(-55, 10.2) * mm});
            skLineSegment(sketch, "E88.left", {"start": v(-45, 100) * mm, "end": v(-45, 10.2) * mm});
            skLineSegment(sketch, "E88.right", {"start": v(-55, 100) * mm, "end": v(-55, 10.2) * mm});
            skSolve(sketch);
        }
        {
            var Q0;
            Q0 = qSketchRegion(id + "F54", true);
            extrude(context, id + "F55", {"entities" : qUnion([Q0]), "operationType" : NewBodyOperationType.REMOVE, "oppositeDirection" : true, "depth" : 5 * mm});
        }
        {
            var Q0;
            {var subQ0=sQuery(id+"F13.wireOp",EDGE,"E10.right");var subQ1=sQuery(id+"F13.wireOp",EDGE,"E10.top");Q0=makeQuery(id+"F22.boolean.opBoolean","SPLIT",EDGE,{"disambiguationData":[TD([makeQuery(id+"F14.opExtrude","SWEPT_FACE",FACE,{"disambiguationData":[OSD([subQ0])]})])],"derivedFrom":makeQuery(id+"F14.opExtrude","CAP_EDGE",EDGE,{"disambiguationData":[OSD([subQ1])],"isStart":true})});}
            var Q1;
            {var subQ0=sQuery(id+"F13.wireOp",EDGE,"E10.left");var subQ1=sQuery(id+"F13.wireOp",EDGE,"E10.top");Q1=makeQuery(id+"F22.boolean.opBoolean","SPLIT",EDGE,{"disambiguationData":[TD([makeQuery(id+"F14.opExtrude","SWEPT_FACE",FACE,{"disambiguationData":[OSD([subQ0])]})])],"derivedFrom":makeQuery(id+"F14.opExtrude","CAP_EDGE",EDGE,{"disambiguationData":[OSD([subQ1])],"isStart":true})});}
            var Q2;
            {var subQ0=sQuery(id+"F13.wireOp",EDGE,"E10.left");var subQ1=sQuery(id+"F13.wireOp",EDGE,"E10.top");Q2=makeQuery(id+"F22.boolean.opBoolean","SPLIT",EDGE,{"disambiguationData":[TD([makeQuery(id+"F14.opExtrude","SWEPT_FACE",FACE,{"disambiguationData":[OSD([subQ0])]})])],"derivedFrom":makeQuery(id+"F14.opExtrude","CAP_EDGE",EDGE,{"disambiguationData":[OSD([subQ1])],"isStart":false})});}
            var Q3;
            {var subQ0=sQuery(id+"F13.wireOp",EDGE,"E10.right");var subQ1=sQuery(id+"F13.wireOp",EDGE,"E10.top");Q3=makeQuery(id+"F22.boolean.opBoolean","SPLIT",EDGE,{"disambiguationData":[TD([makeQuery(id+"F14.opExtrude","SWEPT_FACE",FACE,{"disambiguationData":[OSD([subQ0])]})])],"derivedFrom":makeQuery(id+"F14.opExtrude","CAP_EDGE",EDGE,{"disambiguationData":[OSD([subQ1])],"isStart":false})});}
            var Q4;
            {var subQ0=sQuery(id+"F13.wireOp",EDGE,"E10.bottom");Q4=makeQuery(id+"F14.opExtrude","CAP_EDGE",EDGE,{"disambiguationData":[OSD([subQ0]),TDD([makeQuery(id+"F13.imprint","IMPRINT",EDGE,{"disambiguationData":[TD([[makeQuery(id+"F13.imprint","INTERSECT",VERTEX,{"derivedFrom":[makeQuery(id+"F4.boolean.opBoolean","COPY",EDGE,{"derivedFrom":makeQuery(id+"F4.opExtrude","SWEPT_EDGE",EDGE,{"disambiguationData":[OSD([sQuery(id+"F1.wireOp",EDGE,"E0.top"),sQuery(id+"F3.wireOp",EDGE,"E4.bottom"),sQuery(id+"F3.wireOp",EDGE,"E4.right")])]})}),subQ0]}),-1.0],[makeQuery(id+"F13.imprint","INTERSECT",VERTEX,{"derivedFrom":[subQ0,sQuery(id+"F13.wireOp",EDGE,"E10.right")]}),1.0]])],"derivedFrom":subQ0})])],"isStart":true});}
            var Q5;
            {var subQ0=sQuery(id+"F13.wireOp",EDGE,"E10.bottom");Q5=makeQuery(id+"F14.opExtrude","CAP_EDGE",EDGE,{"disambiguationData":[OSD([subQ0]),TDD([makeQuery(id+"F13.imprint","IMPRINT",EDGE,{"disambiguationData":[TD([[makeQuery(id+"F13.imprint","INTERSECT",VERTEX,{"derivedFrom":[makeQuery(id+"F4.boolean.opBoolean","COPY",EDGE,{"derivedFrom":makeQuery(id+"F4.opExtrude","SWEPT_EDGE",EDGE,{"disambiguationData":[OSD([sQuery(id+"F1.wireOp",EDGE,"E0.top"),sQuery(id+"F3.wireOp",EDGE,"E3.bottom"),sQuery(id+"F3.wireOp",EDGE,"E3.right")])]})}),subQ0]}),1.0],[makeQuery(id+"F13.imprint","INTERSECT",VERTEX,{"derivedFrom":[subQ0,sQuery(id+"F13.wireOp",EDGE,"E10.left")]}),-1.0]])],"derivedFrom":subQ0})])],"isStart":true});}
            var Q6;
            {var subQ0=sQuery(id+"F13.wireOp",EDGE,"E10.bottom");Q6=makeQuery(id+"F14.opExtrude","CAP_EDGE",EDGE,{"disambiguationData":[OSD([subQ0]),TDD([makeQuery(id+"F13.imprint","IMPRINT",EDGE,{"disambiguationData":[TD([[makeQuery(id+"F13.imprint","INTERSECT",VERTEX,{"derivedFrom":[makeQuery(id+"F4.boolean.opBoolean","COPY",EDGE,{"derivedFrom":makeQuery(id+"F4.opExtrude","SWEPT_EDGE",EDGE,{"disambiguationData":[OSD([sQuery(id+"F1.wireOp",EDGE,"E0.top"),sQuery(id+"F3.wireOp",EDGE,"E3.bottom"),sQuery(id+"F3.wireOp",EDGE,"E3.right")])]})}),subQ0]}),1.0],[makeQuery(id+"F13.imprint","INTERSECT",VERTEX,{"derivedFrom":[subQ0,sQuery(id+"F13.wireOp",EDGE,"E10.left")]}),-1.0]])],"derivedFrom":subQ0})])],"isStart":false});}
            var Q7;
            {var subQ0=sQuery(id+"F13.wireOp",EDGE,"E10.bottom");Q7=makeQuery(id+"F14.opExtrude","CAP_EDGE",EDGE,{"disambiguationData":[OSD([subQ0]),TDD([makeQuery(id+"F13.imprint","IMPRINT",EDGE,{"disambiguationData":[TD([[makeQuery(id+"F13.imprint","INTERSECT",VERTEX,{"derivedFrom":[makeQuery(id+"F4.boolean.opBoolean","COPY",EDGE,{"derivedFrom":makeQuery(id+"F4.opExtrude","SWEPT_EDGE",EDGE,{"disambiguationData":[OSD([sQuery(id+"F1.wireOp",EDGE,"E0.top"),sQuery(id+"F3.wireOp",EDGE,"E4.bottom"),sQuery(id+"F3.wireOp",EDGE,"E4.right")])]})}),subQ0]}),-1.0],[makeQuery(id+"F13.imprint","INTERSECT",VERTEX,{"derivedFrom":[subQ0,sQuery(id+"F13.wireOp",EDGE,"E10.right")]}),1.0]])],"derivedFrom":subQ0})])],"isStart":false});}
            fillet(context, id + "F56", {"entities" : qUnion([Q0, Q1, Q2, Q3, Q4, Q5, Q6, Q7]), "radius" : 5 * mm, "tangentPropagation" : true, "allowEdgeOverflow" : false});
        }
        {
            var Q0;
            {var subQ0=sQuery(id+"F32.wireOp",EDGE,"E43.0");var subQ1=sQuery(id+"F32.wireOp",EDGE,"E44.right");Q0=makeQuery(id+"F35.boolean.opBoolean","SPLIT",EDGE,{"disambiguationData":[TD([makeQuery(id+"F33.opExtrude","SWEPT_FACE",FACE,{"disambiguationData":[OSD([subQ1])]})])],"derivedFrom":makeQuery(id+"F33.opExtrude","CAP_EDGE",EDGE,{"disambiguationData":[OSD([subQ0])],"isStart":true})});}
            var Q1;
            {var subQ0=sQuery(id+"F32.wireOp",EDGE,"E43.0");var subQ1=sQuery(id+"F32.wireOp",EDGE,"E44.left");Q1=makeQuery(id+"F35.boolean.opBoolean","SPLIT",EDGE,{"disambiguationData":[TD([makeQuery(id+"F33.opExtrude","SWEPT_FACE",FACE,{"disambiguationData":[OSD([subQ1])]})])],"derivedFrom":makeQuery(id+"F33.opExtrude","CAP_EDGE",EDGE,{"disambiguationData":[OSD([subQ0])],"isStart":true})});}
            var Q2;
            {var subQ0=sQuery(id+"F32.wireOp",EDGE,"E44.left");var subQ1=sQuery(id+"F32.wireOp",EDGE,"E44.top");Q2=makeQuery(id+"F35.boolean.opBoolean","SPLIT",EDGE,{"disambiguationData":[TD([makeQuery(id+"F33.opExtrude","SWEPT_FACE",FACE,{"disambiguationData":[OSD([subQ0])]})])],"derivedFrom":makeQuery(id+"F33.opExtrude","CAP_EDGE",EDGE,{"disambiguationData":[OSD([subQ1])],"isStart":true})});}
            var Q3;
            {var subQ0=sQuery(id+"F32.wireOp",EDGE,"E44.right");var subQ1=sQuery(id+"F32.wireOp",EDGE,"E44.top");Q3=makeQuery(id+"F35.boolean.opBoolean","SPLIT",EDGE,{"disambiguationData":[TD([makeQuery(id+"F33.opExtrude","SWEPT_FACE",FACE,{"disambiguationData":[OSD([subQ0])]})])],"derivedFrom":makeQuery(id+"F33.opExtrude","CAP_EDGE",EDGE,{"disambiguationData":[OSD([subQ1])],"isStart":true})});}
            var Q4;
            {var subQ0=sQuery(id+"F32.wireOp",EDGE,"E43.0");var subQ1=sQuery(id+"F32.wireOp",EDGE,"E44.left");Q4=makeQuery(id+"F35.boolean.opBoolean","SPLIT",EDGE,{"disambiguationData":[TD([makeQuery(id+"F33.opExtrude","SWEPT_FACE",FACE,{"disambiguationData":[OSD([subQ1])]})])],"derivedFrom":makeQuery(id+"F33.opExtrude","CAP_EDGE",EDGE,{"disambiguationData":[OSD([subQ0])],"isStart":false})});}
            var Q5;
            {var subQ0=sQuery(id+"F32.wireOp",EDGE,"E43.0");var subQ1=sQuery(id+"F32.wireOp",EDGE,"E44.right");Q5=makeQuery(id+"F35.boolean.opBoolean","SPLIT",EDGE,{"disambiguationData":[TD([makeQuery(id+"F33.opExtrude","SWEPT_FACE",FACE,{"disambiguationData":[OSD([subQ1])]})])],"derivedFrom":makeQuery(id+"F33.opExtrude","CAP_EDGE",EDGE,{"disambiguationData":[OSD([subQ0])],"isStart":false})});}
            var Q6;
            {var subQ0=sQuery(id+"F32.wireOp",EDGE,"E44.right");var subQ1=sQuery(id+"F32.wireOp",EDGE,"E44.top");Q6=makeQuery(id+"F35.boolean.opBoolean","SPLIT",EDGE,{"disambiguationData":[TD([makeQuery(id+"F33.opExtrude","SWEPT_FACE",FACE,{"disambiguationData":[OSD([subQ0])]})])],"derivedFrom":makeQuery(id+"F33.opExtrude","CAP_EDGE",EDGE,{"disambiguationData":[OSD([subQ1])],"isStart":false})});}
            var Q7;
            {var subQ0=sQuery(id+"F32.wireOp",EDGE,"E44.left");var subQ1=sQuery(id+"F32.wireOp",EDGE,"E44.top");Q7=makeQuery(id+"F35.boolean.opBoolean","SPLIT",EDGE,{"disambiguationData":[TD([makeQuery(id+"F33.opExtrude","SWEPT_FACE",FACE,{"disambiguationData":[OSD([subQ0])]})])],"derivedFrom":makeQuery(id+"F33.opExtrude","CAP_EDGE",EDGE,{"disambiguationData":[OSD([subQ1])],"isStart":false})});}
            fillet(context, id + "F57", {"entities" : qUnion([Q0, Q1, Q2, Q3, Q4, Q5, Q6, Q7]), "radius" : 5 * mm, "tangentPropagation" : true, "allowEdgeOverflow" : false});
        }
        {
            var Q0;
            Q0=makeQuery(id+"F43.opExtrude","CAP_FACE",FACE,{"disambiguationData":[OSD([sQuery(id+"F42.wireOp",EDGE,"E65.bottom"),sQuery(id+"F42.wireOp",EDGE,"E65.top"),sQuery(id+"F42.wireOp",EDGE,"E65.left"),sQuery(id+"F42.wireOp",EDGE,"E65.right")])],"isStart":false});
            var sketch = newSketch(context, id + "F58", { "sketchPlane" : qUnion([Q0])});
            skLineSegment(sketch, "E89.bottom", {"start": v(55, -44.8) * mm, "end": v(-55, -44.8) * mm});
            skLineSegment(sketch, "E89.top", {"start": v(55, 44.8) * mm, "end": v(-55, 44.8) * mm});
            skLineSegment(sketch, "E89.left", {"start": v(55, -44.8) * mm, "end": v(55, 44.8) * mm});
            skLineSegment(sketch, "E89.right", {"start": v(-55, -44.8) * mm, "end": v(-55, 44.8) * mm});
            skSolve(sketch);
        }
        {
            var Q0;
            Q0 = qSketchRegion(id + "F58", true);
            extrude(context, id + "F59", {"entities" : qUnion([Q0]), "operationType" : NewBodyOperationType.REMOVE, "oppositeDirection" : true, "depth" : 5 * mm});
        }
        {
            var Q0;
            {var subQ0=sQuery(id+"F1.wireOp",EDGE,"E0.top");var subQ1=sQuery(id+"F1.wireOp",EDGE,"E0.bottom");var subQ2=sQuery(id+"F1.wireOp",EDGE,"E0.left");var subQ3=sQuery(id+"F1.wireOp",EDGE,"E0.right");Q0=makeQuery(id+"F30.boolean.opBoolean","SPLIT",FACE,{"disambiguationData":[TD([makeQuery(id+"F2.opExtrude","SWEPT_FACE",FACE,{"disambiguationData":[OSD([subQ1])]})])],"derivedFrom":makeQuery(id+"F2.opExtrude","CAP_FACE",FACE,{"disambiguationData":[OSD([subQ1,subQ0,subQ2,subQ3])],"isStart":false})});}
            var sketch = newSketch(context, id + "F60", { "sketchPlane" : qUnion([Q0])});
            skLineSegment(sketch, "E90.bottom", {"start": v(-55, 19.2) * mm, "end": v(55, 19.2) * mm});
            skLineSegment(sketch, "E90.top", {"start": v(-55, -39.8) * mm, "end": v(55, -39.8) * mm});
            skLineSegment(sketch, "E90.left", {"start": v(-55, 19.2) * mm, "end": v(-55, -39.8) * mm});
            skLineSegment(sketch, "E90.right", {"start": v(55, 19.2) * mm, "end": v(55, -39.8) * mm});
            skLineSegment(sketch, "E91.bottom", {"start": v(11.8, 55) * mm, "end": v(34.8, 55) * mm});
            skLineSegment(sketch, "E91.top", {"start": v(11.8, -55) * mm, "end": v(34.8, -55) * mm});
            skLineSegment(sketch, "E91.left", {"start": v(11.8, 55) * mm, "end": v(11.8, -55) * mm});
            skLineSegment(sketch, "E91.right", {"start": v(34.8, 55) * mm, "end": v(34.8, -55) * mm});
            skLineSegment(sketch, "E92.bottom", {"start": v(34.8, 34.8) * mm, "end": v(55, 34.8) * mm});
            skLineSegment(sketch, "E92.top", {"start": v(34.8, -39.8) * mm, "end": v(55, -39.8) * mm});
            skLineSegment(sketch, "E92.left", {"start": v(34.8, 34.8) * mm, "end": v(34.8, -39.8) * mm});
            skLineSegment(sketch, "E92.right", {"start": v(55, 34.8) * mm, "end": v(55, -39.8) * mm});
            skLineSegment(sketch, "E93.bottom", {"start": v(-35.9, -39.8) * mm, "end": v(11.8, -39.8) * mm});
            skLineSegment(sketch, "E93.top", {"start": v(-35.9, -55) * mm, "end": v(11.8, -55) * mm});
            skLineSegment(sketch, "E93.left", {"start": v(-35.9, -39.8) * mm, "end": v(-35.9, -55) * mm});
            skLineSegment(sketch, "E93.right", {"start": v(11.8, -39.8) * mm, "end": v(11.8, -55) * mm});
            skSolve(sketch);
        }
        {
            var Q0;
            Q0 = qSketchRegion(id + "F60", true);
            extrude(context, id + "F61", {"entities" : qUnion([Q0]), "operationType" : NewBodyOperationType.REMOVE, "oppositeDirection" : true, "depth" : 5 * mm});
        }
        {
            var Q0;
            Q0=makeQuery(id+"F61.boolean.opBoolean","COPY",FACE,{"derivedFrom":makeQuery(id+"F61.opExtrude","CAP_FACE",FACE,{"disambiguationData":[OSD([sQuery(id+"F60.wireOp",EDGE,"E90.bottom"),sQuery(id+"F60.wireOp",EDGE,"E90.top"),sQuery(id+"F60.wireOp",EDGE,"E90.left"),sQuery(id+"F60.wireOp",EDGE,"E91.bottom"),sQuery(id+"F60.wireOp",EDGE,"E91.top"),sQuery(id+"F60.wireOp",EDGE,"E91.left"),sQuery(id+"F60.wireOp",EDGE,"E91.right"),sQuery(id+"F60.wireOp",EDGE,"E92.bottom"),sQuery(id+"F60.wireOp",EDGE,"E92.top"),sQuery(id+"F60.wireOp",EDGE,"E92.right"),sQuery(id+"F60.wireOp",EDGE,"E93.top"),sQuery(id+"F60.wireOp",EDGE,"E93.left")])],"isStart":false})});
            var sketch = newSketch(context, id + "F62", { "sketchPlane" : qUnion([Q0])});
            skLineSegment(sketch, "E94.bottom", {"start": v(-53, 15.58) * mm, "end": v(7, 15.58) * mm});
            skLineSegment(sketch, "E94.top", {"start": v(-53, -35.42) * mm, "end": v(7, -35.42) * mm});
            skLineSegment(sketch, "E94.left", {"start": v(-53, 15.58) * mm, "end": v(-53, -35.42) * mm});
            skLineSegment(sketch, "E94.right", {"start": v(7, 15.58) * mm, "end": v(7, -35.42) * mm});
            skSolve(sketch);
        }
        {
            var Q0;
            Q0 = qSketchRegion(id + "F62", true);
            extrude(context, id + "F63", {"entities" : qUnion([Q0]), "operationType" : NewBodyOperationType.REMOVE, "oppositeDirection" : true, "depth" : 2 * mm});
        }
        {
            var Q0;
            Q0=makeQuery(id+"F61.boolean.opBoolean","COPY",FACE,{"derivedFrom":makeQuery(id+"F61.opExtrude","CAP_FACE",FACE,{"disambiguationData":[OSD([sQuery(id+"F60.wireOp",EDGE,"E90.bottom"),sQuery(id+"F60.wireOp",EDGE,"E90.top"),sQuery(id+"F60.wireOp",EDGE,"E90.left"),sQuery(id+"F60.wireOp",EDGE,"E91.bottom"),sQuery(id+"F60.wireOp",EDGE,"E91.top"),sQuery(id+"F60.wireOp",EDGE,"E91.left"),sQuery(id+"F60.wireOp",EDGE,"E91.right"),sQuery(id+"F60.wireOp",EDGE,"E92.bottom"),sQuery(id+"F60.wireOp",EDGE,"E92.top"),sQuery(id+"F60.wireOp",EDGE,"E92.right"),sQuery(id+"F60.wireOp",EDGE,"E93.top"),sQuery(id+"F60.wireOp",EDGE,"E93.left")])],"isStart":false})});
            var sketch = newSketch(context, id + "F64", { "sketchPlane" : qUnion([Q0])});
            skCircle(sketch, "E95", {"center": v(31.5, 0) * mm, "radius": 18 * mm});
            skCircle(sketch, "E96", {"center": v(31.5, 0) * mm, "radius": 23.5 * mm});
            skCircle(sketch, "E97", {"center": v(31.5, 0) * mm, "radius": 22.5 * mm});
            skLineSegment(sketch, "E98.0", {"start": v(34.8, 55) * mm, "end": v(11.8, 55) * mm});
            skSolve(sketch);
        }
        {
            var Q0;
            Q0=makeQuery(id+"F64.imprint","IMPRINT",FACE,{"disambiguationData":[TD([[makeQuery(id+"F64.imprint","IMPRINT",EDGE,{"derivedFrom":sQuery(id+"F64.wireOp",EDGE,"E95")}),1.0]])]});
            extrude(context, id + "F65", {"entities" : qUnion([Q0]), "operationType" : NewBodyOperationType.REMOVE, "oppositeDirection" : true, "depth" : 5 * mm});
        }
        {
            var Q0;
            Q0 = qSketchRegion(id + "F64", true);
            extrude(context, id + "F66", {"entities" : qUnion([Q0]), "operationType" : NewBodyOperationType.ADD, "depth" : 5 * mm});
        }
        {
            var Q0;
            {var subQ0=sQuery(id+"F1.wireOp",EDGE,"E0.top");var subQ2=makeQuery(id+"F2.opExtrude","CAP_EDGE",EDGE,{"disambiguationData":[OSD([subQ0])],"isStart":false});Q0=makeQuery(id+"F61.boolean.opBoolean","SPLIT",EDGE,{"disambiguationData":[TD([makeQuery(id+"F4.boolean.opBoolean","COPY",FACE,{"derivedFrom":makeQuery(id+"F4.opExtrude","SWEPT_FACE",FACE,{"disambiguationData":[OSD([sQuery(id+"F3.wireOp",EDGE,"E4.right")])]})})])],"derivedFrom":subQ2});}
            var Q1;
            {var subQ0=sQuery(id+"F1.wireOp",EDGE,"E0.top");Q1=makeQuery(id+"F61.boolean.opBoolean","SPLIT",EDGE,{"disambiguationData":[TD([makeQuery(id+"F4.boolean.opBoolean","COPY",FACE,{"derivedFrom":makeQuery(id+"F4.opExtrude","SWEPT_FACE",FACE,{"disambiguationData":[OSD([sQuery(id+"F3.wireOp",EDGE,"E3.right")])]})})])],"derivedFrom":makeQuery(id+"F2.opExtrude","CAP_EDGE",EDGE,{"disambiguationData":[OSD([subQ0])],"isStart":false})});}
            var Q2;
            {var subQ0=sQuery(id+"F1.wireOp",EDGE,"E0.bottom");Q2=makeQuery(id+"F61.boolean.opBoolean","SPLIT",EDGE,{"disambiguationData":[TD([makeQuery(id+"F4.boolean.opBoolean","COPY",FACE,{"derivedFrom":makeQuery(id+"F4.opExtrude","SWEPT_FACE",FACE,{"disambiguationData":[OSD([sQuery(id+"F3.wireOp",EDGE,"E2.right")])]})})])],"derivedFrom":makeQuery(id+"F2.opExtrude","CAP_EDGE",EDGE,{"disambiguationData":[OSD([subQ0])],"isStart":false})});}
            var Q3;
            {var subQ0=sQuery(id+"F1.wireOp",EDGE,"E0.bottom");var subQ2=makeQuery(id+"F2.opExtrude","CAP_EDGE",EDGE,{"disambiguationData":[OSD([subQ0])],"isStart":false});Q3=makeQuery(id+"F61.boolean.opBoolean","SPLIT",EDGE,{"disambiguationData":[TD([makeQuery(id+"F4.boolean.opBoolean","COPY",FACE,{"derivedFrom":makeQuery(id+"F4.opExtrude","SWEPT_FACE",FACE,{"disambiguationData":[OSD([sQuery(id+"F3.wireOp",EDGE,"E1.right")])]})})])],"derivedFrom":subQ2});}
            var Q4;
            {var subQ0=sQuery(id+"F13.wireOp",EDGE,"E10.bottom");Q4=makeQuery(id+"F14.opExtrude","CAP_EDGE",EDGE,{"disambiguationData":[OSD([subQ0]),TDD([makeQuery(id+"F13.imprint","IMPRINT",EDGE,{"disambiguationData":[TD([[makeQuery(id+"F13.imprint","INTERSECT",VERTEX,{"derivedFrom":[makeQuery(id+"F4.boolean.opBoolean","COPY",EDGE,{"derivedFrom":makeQuery(id+"F4.opExtrude","SWEPT_EDGE",EDGE,{"disambiguationData":[OSD([sQuery(id+"F1.wireOp",EDGE,"E0.top"),sQuery(id+"F3.wireOp",EDGE,"E4.bottom"),sQuery(id+"F3.wireOp",EDGE,"E4.right")])]})}),subQ0]}),-1.0],[makeQuery(id+"F13.imprint","INTERSECT",VERTEX,{"derivedFrom":[subQ0,sQuery(id+"F13.wireOp",EDGE,"E10.right")]}),1.0]])],"derivedFrom":subQ0})])],"isStart":false});}
            var Q5;
            {var subQ0=sQuery(id+"F13.wireOp",EDGE,"E10.bottom");Q5=makeQuery(id+"F14.opExtrude","CAP_EDGE",EDGE,{"disambiguationData":[OSD([subQ0]),TDD([makeQuery(id+"F13.imprint","IMPRINT",EDGE,{"disambiguationData":[TD([[makeQuery(id+"F13.imprint","INTERSECT",VERTEX,{"derivedFrom":[makeQuery(id+"F4.boolean.opBoolean","COPY",EDGE,{"derivedFrom":makeQuery(id+"F4.opExtrude","SWEPT_EDGE",EDGE,{"disambiguationData":[OSD([sQuery(id+"F1.wireOp",EDGE,"E0.top"),sQuery(id+"F3.wireOp",EDGE,"E3.bottom"),sQuery(id+"F3.wireOp",EDGE,"E3.right")])]})}),subQ0]}),1.0],[makeQuery(id+"F13.imprint","INTERSECT",VERTEX,{"derivedFrom":[subQ0,sQuery(id+"F13.wireOp",EDGE,"E10.left")]}),-1.0]])],"derivedFrom":subQ0})])],"isStart":true});}
            var Q6;
            {var subQ0=sQuery(id+"F13.wireOp",EDGE,"E10.bottom");Q6=makeQuery(id+"F14.opExtrude","CAP_EDGE",EDGE,{"disambiguationData":[OSD([subQ0]),TDD([makeQuery(id+"F13.imprint","IMPRINT",EDGE,{"disambiguationData":[TD([[makeQuery(id+"F13.imprint","INTERSECT",VERTEX,{"derivedFrom":[makeQuery(id+"F4.boolean.opBoolean","COPY",EDGE,{"derivedFrom":makeQuery(id+"F4.opExtrude","SWEPT_EDGE",EDGE,{"disambiguationData":[OSD([sQuery(id+"F1.wireOp",EDGE,"E0.top"),sQuery(id+"F3.wireOp",EDGE,"E4.bottom"),sQuery(id+"F3.wireOp",EDGE,"E4.right")])]})}),subQ0]}),-1.0],[makeQuery(id+"F13.imprint","INTERSECT",VERTEX,{"derivedFrom":[subQ0,sQuery(id+"F13.wireOp",EDGE,"E10.right")]}),1.0]])],"derivedFrom":subQ0})])],"isStart":true});}
            fillet(context, id + "F67", {"entities" : qUnion([Q0, Q1, Q2, Q3, Q4, Q5, Q6]), "radius" : 5 * mm, "tangentPropagation" : true, "allowEdgeOverflow" : false});
        }
        {
            var Q0;
            Q0=makeQuery(id+"F33.opExtrude","CAP_FACE",FACE,{"disambiguationData":[OSD([sQuery(id+"F32.wireOp",EDGE,"E43.0"),sQuery(id+"F32.wireOp",EDGE,"E44.top"),sQuery(id+"F32.wireOp",EDGE,"E44.left"),sQuery(id+"F32.wireOp",EDGE,"E44.right")])],"isStart":false});
            var sketch = newSketch(context, id + "F68", { "sketchPlane" : qUnion([Q0])});
            skLineSegment(sketch, "E99.bottom", {"start": v(45, 10) * mm, "end": v(-20, 10) * mm});
            skLineSegment(sketch, "E99.top", {"start": v(45, 30) * mm, "end": v(-20, 30) * mm});
            skLineSegment(sketch, "E99.left", {"start": v(45, 10) * mm, "end": v(45, 30) * mm});
            skLineSegment(sketch, "E99.right", {"start": v(-20, 10) * mm, "end": v(-20, 30) * mm});
            skSolve(sketch);
        }
        {
            var Q0;
            Q0=makeQuery(id+"F68.imprint","IMPRINT",FACE,{"disambiguationData":[TD([[makeQuery(id+"F68.imprint","IMPRINT",EDGE,{"derivedFrom":sQuery(id+"F68.wireOp",EDGE,"E99.bottom")}),1.0]])]});
            var Q1;
            Q1=sQuery(id+"F68.wireOp",EDGE,"E99.right");
            extrude(context, id + "F69", {"entities" : qUnion([Q0]), "operationType" : NewBodyOperationType.REMOVE, "surfaceEntities" : qUnion([Q1]), "oppositeDirection" : true, "depth" : 5 * mm});
        }
        {
            var Q0;
            Q0=qCreatedBy(makeId("Top.planeOp"),FACE);
            var sketch = newSketch(context, id + "F70", { "sketchPlane" : qUnion([Q0])});
            skLineSegment(sketch, "E100.top", {"start": v(-2.67, -32.73) * mm, "end": v(-53.67, -32.73) * mm, "construction": true});
            skLineSegment(sketch, "E100.left", {"start": v(-2.67, 48.27) * mm, "end": v(-2.67, -32.73) * mm, "construction": true});
            skLineSegment(sketch, "E100.right", {"start": v(-53.67, 28.27) * mm, "end": v(-53.67, -32.73) * mm, "construction": true});
            skLineSegment(sketch, "E101.bottom", {"start": v(56.33, 28.27) * mm, "end": v(5.33, 28.27) * mm, "construction": true});
            skLineSegment(sketch, "E101.top", {"start": v(56.33, -32.73) * mm, "end": v(5.33, -32.73) * mm});
            skLineSegment(sketch, "E101.right", {"start": v(5.33, 28.27) * mm, "end": v(5.33, -32.73) * mm, "construction": true});
            skLineSegment(sketch, "E102", {"start": v(-28.17, -32.73) * mm, "end": v(-28.16, 28.27) * mm, "construction": true});
            skLineSegment(sketch, "E103", {"start": v(30.83, -32.73) * mm, "end": v(30.83, 28.27) * mm, "construction": true});
            skLineSegment(sketch, "E104", {"start": v(56.33, 28.27) * mm, "end": v(56.33, -32.73) * mm, "construction": true});
            skLineSegment(sketch, "E105.bottom", {"start": v(56.33, -37.23) * mm, "end": v(46.33, -37.23) * mm, "construction": true});
            skLineSegment(sketch, "E105.top", {"start": v(56.33, -47.23) * mm, "end": v(46.33, -47.23) * mm, "construction": true});
            skLineSegment(sketch, "E105.left", {"start": v(56.33, -37.23) * mm, "end": v(56.33, -47.23) * mm, "construction": true});
            skLineSegment(sketch, "E105.right", {"start": v(46.33, -37.23) * mm, "end": v(46.33, -47.23) * mm, "construction": true});
            skLineSegment(sketch, "E106.bottom", {"start": v(56.33, 42.77) * mm, "end": v(46.33, 42.77) * mm, "construction": true});
            skLineSegment(sketch, "E106.top", {"start": v(56.33, 32.77) * mm, "end": v(46.33, 32.77) * mm, "construction": true});
            skLineSegment(sketch, "E106.left", {"start": v(56.33, 42.77) * mm, "end": v(56.33, 32.77) * mm, "construction": true});
            skLineSegment(sketch, "E106.right", {"start": v(46.33, 42.77) * mm, "end": v(46.33, 32.77) * mm, "construction": true});
            skLineSegment(sketch, "E107", {"start": v(56.33, -32.73) * mm, "end": v(56.33, -37.23) * mm, "construction": true});
            skLineSegment(sketch, "E108", {"start": v(56.33, 28.27) * mm, "end": v(56.33, 32.77) * mm, "construction": true});
            skLineSegment(sketch, "E109", {"start": v(-53.67, -32.73) * mm, "end": v(-53.67, -37.23) * mm, "construction": true});
            skLineSegment(sketch, "E110", {"start": v(-53.67, 28.27) * mm, "end": v(-53.67, 32.77) * mm, "construction": true});
            skLineSegment(sketch, "E111.bottom", {"start": v(-53.67, -37.23) * mm, "end": v(-43.67, -37.23) * mm, "construction": true});
            skLineSegment(sketch, "E111.top", {"start": v(-53.67, -47.23) * mm, "end": v(-43.67, -47.23) * mm, "construction": true});
            skLineSegment(sketch, "E111.left", {"start": v(-53.67, -37.23) * mm, "end": v(-53.67, -47.23) * mm, "construction": true});
            skLineSegment(sketch, "E111.right", {"start": v(-43.67, -37.23) * mm, "end": v(-43.67, -47.23) * mm, "construction": true});
            skLineSegment(sketch, "E112.bottom", {"start": v(-53.67, 32.77) * mm, "end": v(-43.67, 32.77) * mm, "construction": true});
            skLineSegment(sketch, "E112.top", {"start": v(-53.67, 42.77) * mm, "end": v(-43.67, 42.77) * mm, "construction": true});
            skLineSegment(sketch, "E112.left", {"start": v(-53.67, 32.77) * mm, "end": v(-53.67, 42.77) * mm, "construction": true});
            skLineSegment(sketch, "E112.right", {"start": v(-43.67, 32.77) * mm, "end": v(-43.67, 42.77) * mm, "construction": true});
            skLineSegment(sketch, "E113", {"start": v(30.83, -2.23) * mm, "end": v(30.83, -39.08) * mm, "construction": true});
            skLineSegment(sketch, "E114", {"start": v(30.83, -2.23) * mm, "end": v(30.83, 34.62) * mm, "construction": true});
            skLineSegment(sketch, "E115", {"start": v(-28.17, -2.23) * mm, "end": v(-28.17, -39.08) * mm, "construction": true});
            skLineSegment(sketch, "E116", {"start": v(-28.17, -2.23) * mm, "end": v(-28.16, 34.62) * mm, "construction": true});
            skPoint(sketch, "E117.middle", {"position": v(-28.17, -2.23) * mm});
            skPoint(sketch, "E118.middle", {"position": v(30.83, -2.23) * mm});
            skCircle(sketch, "E119", {"center": v(-28.17, -39.08) * mm, "radius": 1.5 * mm});
            skLineSegment(sketch, "E120.bottom", {"start": v(-53.67, 42.77) * mm, "end": v(-43.67, 42.77) * mm});
            skLineSegment(sketch, "E120.top", {"start": v(-53.67, 32.77) * mm, "end": v(-43.67, 32.77) * mm});
            skLineSegment(sketch, "E120.left", {"start": v(-53.67, 42.77) * mm, "end": v(-53.67, 32.77) * mm});
            skLineSegment(sketch, "E120.right", {"start": v(-43.67, 42.77) * mm, "end": v(-43.67, 32.77) * mm});
            skLineSegment(sketch, "E121.bottom", {"start": v(-53.67, -47.23) * mm, "end": v(-43.67, -47.23) * mm});
            skLineSegment(sketch, "E121.top", {"start": v(-53.67, -37.23) * mm, "end": v(-43.67, -37.23) * mm});
            skLineSegment(sketch, "E121.left", {"start": v(-53.67, -47.23) * mm, "end": v(-53.67, -37.23) * mm});
            skLineSegment(sketch, "E121.right", {"start": v(-43.67, -47.23) * mm, "end": v(-43.67, -37.23) * mm});
            skLineSegment(sketch, "E122.bottom", {"start": v(46.33, -47.23) * mm, "end": v(56.33, -47.23) * mm});
            skLineSegment(sketch, "E122.top", {"start": v(46.33, -37.23) * mm, "end": v(56.33, -37.23) * mm});
            skLineSegment(sketch, "E122.left", {"start": v(46.33, -47.23) * mm, "end": v(46.33, -37.23) * mm});
            skLineSegment(sketch, "E122.right", {"start": v(56.33, -47.23) * mm, "end": v(56.33, -37.23) * mm});
            skLineSegment(sketch, "E123.bottom", {"start": v(46.33, 32.77) * mm, "end": v(56.33, 32.77) * mm});
            skLineSegment(sketch, "E123.top", {"start": v(46.33, 42.77) * mm, "end": v(56.33, 42.77) * mm});
            skLineSegment(sketch, "E123.left", {"start": v(46.33, 32.77) * mm, "end": v(46.33, 42.77) * mm});
            skLineSegment(sketch, "E123.right", {"start": v(56.33, 32.77) * mm, "end": v(56.33, 42.77) * mm});
            skLineSegment(sketch, "E124.bottom", {"start": v(33.33, 37.77) * mm, "end": v(28.33, 37.77) * mm});
            skLineSegment(sketch, "E124.top", {"start": v(33.33, -42.23) * mm, "end": v(28.33, -42.23) * mm});
            skLineSegment(sketch, "E124.left", {"start": v(33.33, 37.77) * mm, "end": v(33.33, -42.23) * mm});
            skLineSegment(sketch, "E124.right", {"start": v(28.33, 37.77) * mm, "end": v(28.33, -42.23) * mm});
            skPoint(sketch, "E124.cornerSnap0", {"position": v(46.33, 37.77) * mm});
            skLineSegment(sketch, "E125.bottom", {"start": v(-30.67, 37.77) * mm, "end": v(-25.67, 37.77) * mm});
            skLineSegment(sketch, "E125.top", {"start": v(-30.67, -42.23) * mm, "end": v(-25.67, -42.23) * mm});
            skLineSegment(sketch, "E125.left", {"start": v(-30.67, 37.77) * mm, "end": v(-30.67, -42.23) * mm});
            skLineSegment(sketch, "E125.right", {"start": v(-25.67, 37.77) * mm, "end": v(-25.67, -42.23) * mm});
            skPoint(sketch, "E125.cornerSnap0", {"position": v(-43.67, 37.77) * mm});
            skLineSegment(sketch, "E126.bottom", {"start": v(-43.67, 37.77) * mm, "end": v(46.33, 37.77) * mm});
            skLineSegment(sketch, "E126.top", {"start": v(-43.67, 32.77) * mm, "end": v(46.33, 32.77) * mm});
            skLineSegment(sketch, "E126.left", {"start": v(-43.67, 37.77) * mm, "end": v(-43.67, 32.77) * mm});
            skLineSegment(sketch, "E126.right", {"start": v(46.33, 37.77) * mm, "end": v(46.33, 32.77) * mm});
            skLineSegment(sketch, "E127.bottom", {"start": v(-43.67, -37.23) * mm, "end": v(46.33, -37.23) * mm});
            skLineSegment(sketch, "E127.top", {"start": v(-43.67, -42.23) * mm, "end": v(46.33, -42.23) * mm});
            skLineSegment(sketch, "E127.left", {"start": v(-43.67, -37.23) * mm, "end": v(-43.67, -42.23) * mm});
            skLineSegment(sketch, "E127.right", {"start": v(46.33, -37.23) * mm, "end": v(46.33, -42.23) * mm});
            skCircle(sketch, "E128", {"center": v(-28.16, 34.62) * mm, "radius": 1.5 * mm});
            skCircle(sketch, "E129", {"center": v(30.83, 34.62) * mm, "radius": 1.5 * mm});
            skCircle(sketch, "E130", {"center": v(30.83, -39.08) * mm, "radius": 1.5 * mm});
            skLineSegment(sketch, "E131.bottom", {"start": v(-43.67, 35.27) * mm, "end": v(-30.67, 35.27) * mm});
            skLineSegment(sketch, "E131.top", {"start": v(-43.67, 32.77) * mm, "end": v(-30.67, 32.77) * mm});
            skLineSegment(sketch, "E131.left", {"start": v(-43.67, 35.27) * mm, "end": v(-43.67, 32.77) * mm});
            skLineSegment(sketch, "E131.right", {"start": v(-30.67, 35.27) * mm, "end": v(-30.67, 32.77) * mm});
            skSolve(sketch);
        }
        {
            var Q0;
            Q0 = qSketchRegion(id + "F70", true);
            extrude(context, id + "F71", {"entities" : qUnion([Q0]), "depth" : 5 * mm});
        }
        {
            var Q0;
            Q0=makeQuery(id+"F71.opExtrude","CAP_FACE",FACE,{"disambiguationData":[OSD([sQuery(id+"F70.wireOp",EDGE,"4bb4f0b3-457f-41b7-a364-44632f637f0d"),sQuery(id+"F70.wireOp",EDGE,"a850c7fe-6581-45b5-b35d-616f1dfd06d3"),sQuery(id+"F70.wireOp",EDGE,"E119"),sQuery(id+"F70.wireOp",EDGE,"c46ebc12-d630-4f32-affe-7b38bfe806f6"),sQuery(id+"F70.wireOp",EDGE,"E120.bottom"),sQuery(id+"F70.wireOp",EDGE,"E120.top"),sQuery(id+"F70.wireOp",EDGE,"E120.left"),sQuery(id+"F70.wireOp",EDGE,"E120.right"),sQuery(id+"F70.wireOp",EDGE,"E121.bottom"),sQuery(id+"F70.wireOp",EDGE,"E121.top"),sQuery(id+"F70.wireOp",EDGE,"E121.left"),sQuery(id+"F70.wireOp",EDGE,"E121.right"),sQuery(id+"F70.wireOp",EDGE,"E122.bottom"),sQuery(id+"F70.wireOp",EDGE,"E122.top"),sQuery(id+"F70.wireOp",EDGE,"E122.left"),sQuery(id+"F70.wireOp",EDGE,"E122.right"),sQuery(id+"F70.wireOp",EDGE,"E123.bottom"),sQuery(id+"F70.wireOp",EDGE,"E123.top"),sQuery(id+"F70.wireOp",EDGE,"E123.left"),sQuery(id+"F70.wireOp",EDGE,"E123.right"),sQuery(id+"F70.wireOp",EDGE,"E124.left"),sQuery(id+"F70.wireOp",EDGE,"E124.right"),sQuery(id+"F70.wireOp",EDGE,"E125.top"),sQuery(id+"F70.wireOp",EDGE,"E125.left"),sQuery(id+"F70.wireOp",EDGE,"E125.right"),sQuery(id+"F70.wireOp",EDGE,"E126.bottom"),sQuery(id+"F70.wireOp",EDGE,"E126.top"),sQuery(id+"F70.wireOp",EDGE,"E127.bottom"),sQuery(id+"F70.wireOp",EDGE,"E127.top")])],"isStart":true});
            var sketch = newSketch(context, id + "F72", { "sketchPlane" : qUnion([Q0])});
            skLineSegment(sketch, "E132.bottom", {"start": v(46.33, 47.23) * mm, "end": v(56.33, 47.23) * mm});
            skLineSegment(sketch, "E132.top", {"start": v(46.33, 37.23) * mm, "end": v(56.33, 37.23) * mm});
            skLineSegment(sketch, "E132.left", {"start": v(46.33, 47.23) * mm, "end": v(46.33, 37.23) * mm});
            skLineSegment(sketch, "E132.right", {"start": v(56.33, 47.23) * mm, "end": v(56.33, 37.23) * mm});
            skPoint(sketch, "E133.oppositeSnap0", {"position": v(46.33, -40.27) * mm});
            skLineSegment(sketch, "E133.bottom", {"start": v(56.33, -42.77) * mm, "end": v(46.33, -42.77) * mm});
            skLineSegment(sketch, "E133.top", {"start": v(56.33, -32.77) * mm, "end": v(46.33, -32.77) * mm});
            skLineSegment(sketch, "E133.left", {"start": v(56.33, -42.77) * mm, "end": v(56.33, -32.77) * mm});
            skLineSegment(sketch, "E133.right", {"start": v(46.33, -42.77) * mm, "end": v(46.33, -32.77) * mm});
            skPoint(sketch, "E134.oppositeSnap0", {"position": v(-43.67, -40.27) * mm});
            skLineSegment(sketch, "E134.bottom", {"start": v(-53.67, -42.77) * mm, "end": v(-43.67, -42.77) * mm});
            skLineSegment(sketch, "E134.top", {"start": v(-53.67, -32.77) * mm, "end": v(-43.67, -32.77) * mm});
            skLineSegment(sketch, "E134.left", {"start": v(-53.67, -42.77) * mm, "end": v(-53.67, -32.77) * mm});
            skLineSegment(sketch, "E134.right", {"start": v(-43.67, -42.77) * mm, "end": v(-43.67, -32.77) * mm});
            skLineSegment(sketch, "E135.bottom", {"start": v(-53.67, 47.23) * mm, "end": v(-43.67, 47.23) * mm});
            skLineSegment(sketch, "E135.top", {"start": v(-53.67, 37.23) * mm, "end": v(-43.67, 37.23) * mm});
            skLineSegment(sketch, "E135.left", {"start": v(-53.67, 47.23) * mm, "end": v(-53.67, 37.23) * mm});
            skLineSegment(sketch, "E135.right", {"start": v(-43.67, 47.23) * mm, "end": v(-43.67, 37.23) * mm});
            skSolve(sketch);
        }
        {
            var Q0;
            Q0 = qSketchRegion(id + "F72", true);
            extrude(context, id + "F73", {"entities" : qUnion([Q0]), "operationType" : NewBodyOperationType.ADD, "depth" : 5 * mm});
        }
        {
            var Q0;
            Q0=makeQuery(id+"F73.boolean.opBoolean","MERGE",FACE,{"derivedFrom":[makeQuery(id+"F71.opExtrude","SWEPT_FACE",FACE,{"disambiguationData":[OSD([sQuery(id+"F70.wireOp",EDGE,"E123.top")])]}),makeQuery(id+"F73.opExtrude","SWEPT_FACE",FACE,{"disambiguationData":[OSD([sQuery(id+"F72.wireOp",EDGE,"E133.bottom")])]})]});
            var sketch = newSketch(context, id + "F74", { "sketchPlane" : qUnion([Q0])});
            skLineSegment(sketch, "E136.0", {"start": v(-46.33, -5) * mm, "end": v(-56.33, -5) * mm});
            skLineSegment(sketch, "E137.0", {"start": v(-56.33, 5) * mm, "end": v(-56.33, -5) * mm});
            skLineSegment(sketch, "E138.0", {"start": v(53.67, -5) * mm, "end": v(43.67, -5) * mm});
            skLineSegment(sketch, "E139.0", {"start": v(53.67, 5) * mm, "end": v(53.67, -5) * mm});
            skCircle(sketch, "E140", {"center": v(-51.33, 0) * mm, "radius": 2.75 * mm});
            skPoint(sketch, "E140.centerSnap0", {"position": v(-56.33, 0) * mm});
            skPoint(sketch, "E140.centerSnap1", {"position": v(-51.33, -5) * mm});
            skCircle(sketch, "E141", {"center": v(48.67, 0) * mm, "radius": 2.75 * mm});
            skPoint(sketch, "E141.centerSnap0", {"position": v(53.67, 0) * mm});
            skPoint(sketch, "E141.centerSnap1", {"position": v(48.67, -5) * mm});
            skSolve(sketch);
        }
        {
            var Q0;
            Q0 = qSketchRegion(id + "F74", true);
            extrude(context, id + "F75", {"entities" : qUnion([Q0]), "operationType" : NewBodyOperationType.REMOVE, "oppositeDirection" : true, "depth" : 8 * mm});
        }
        {
            var Q0;
            Q0=makeQuery(id+"F73.boolean.opBoolean","MERGE",FACE,{"derivedFrom":[makeQuery(id+"F71.opExtrude","SWEPT_FACE",FACE,{"disambiguationData":[OSD([sQuery(id+"F70.wireOp",EDGE,"E122.bottom")])]}),makeQuery(id+"F73.opExtrude","SWEPT_FACE",FACE,{"disambiguationData":[OSD([sQuery(id+"F72.wireOp",EDGE,"E132.bottom")])]})]});
            var sketch = newSketch(context, id + "F76", { "sketchPlane" : qUnion([Q0])});
            skLineSegment(sketch, "E142.0", {"start": v(56.33, 5) * mm, "end": v(56.33, -5) * mm});
            skLineSegment(sketch, "E143.0", {"start": v(46.33, -5) * mm, "end": v(56.33, -5) * mm});
            skLineSegment(sketch, "E144.0", {"start": v(-53.67, -5) * mm, "end": v(-43.67, -5) * mm});
            skLineSegment(sketch, "E145.0", {"start": v(-53.67, 5) * mm, "end": v(-53.67, -5) * mm});
            skCircle(sketch, "E146", {"center": v(-48.67, 0) * mm, "radius": 2.75 * mm});
            skPoint(sketch, "E146.centerSnap0", {"position": v(-53.67, 0) * mm});
            skPoint(sketch, "E146.centerSnap1", {"position": v(-48.67, -5) * mm});
            skCircle(sketch, "E147", {"center": v(51.33, 0) * mm, "radius": 2.75 * mm});
            skPoint(sketch, "E147.centerSnap0", {"position": v(56.33, 0) * mm});
            skPoint(sketch, "E147.centerSnap1", {"position": v(51.33, -5) * mm});
            skSolve(sketch);
        }
        {
            var Q0;
            Q0 = qSketchRegion(id + "F76", true);
            extrude(context, id + "F77", {"entities" : qUnion([Q0]), "operationType" : NewBodyOperationType.REMOVE, "oppositeDirection" : true, "depth" : 8 * mm});
        }
        {
            var Q0;
            Q0=makeQuery(id+"F71.opExtrude","SWEPT_EDGE",EDGE,{"disambiguationData":[OSD([sQuery(id+"F70.wireOp",EDGE,"E125.right"),sQuery(id+"F70.wireOp",EDGE,"E126.top")])]});
            var Q1;
            Q1=makeQuery(id+"F71.opExtrude","SWEPT_EDGE",EDGE,{"disambiguationData":[OSD([sQuery(id+"F70.wireOp",EDGE,"E125.left"),sQuery(id+"F70.wireOp",EDGE,"E126.top")])]});
            var Q2;
            Q2=makeQuery(id+"F71.opExtrude","SWEPT_EDGE",EDGE,{"disambiguationData":[OSD([sQuery(id+"F70.wireOp",EDGE,"E124.right"),sQuery(id+"F70.wireOp",EDGE,"E126.top")])]});
            var Q3;
            Q3=makeQuery(id+"F71.opExtrude","SWEPT_EDGE",EDGE,{"disambiguationData":[OSD([sQuery(id+"F70.wireOp",EDGE,"E124.left"),sQuery(id+"F70.wireOp",EDGE,"E126.top")])]});
            var Q4;
            Q4=makeQuery(id+"F71.opExtrude","SWEPT_EDGE",EDGE,{"disambiguationData":[OSD([sQuery(id+"F70.wireOp",EDGE,"E124.left"),sQuery(id+"F70.wireOp",EDGE,"E127.bottom")])]});
            var Q5;
            Q5=makeQuery(id+"F71.opExtrude","SWEPT_EDGE",EDGE,{"disambiguationData":[OSD([sQuery(id+"F70.wireOp",EDGE,"E124.right"),sQuery(id+"F70.wireOp",EDGE,"E127.bottom")])]});
            var Q6;
            Q6=makeQuery(id+"F71.opExtrude","SWEPT_EDGE",EDGE,{"disambiguationData":[OSD([sQuery(id+"F70.wireOp",EDGE,"E125.right"),sQuery(id+"F70.wireOp",EDGE,"E127.bottom")])]});
            var Q7;
            Q7=makeQuery(id+"F71.opExtrude","SWEPT_EDGE",EDGE,{"disambiguationData":[OSD([sQuery(id+"F70.wireOp",EDGE,"E125.left"),sQuery(id+"F70.wireOp",EDGE,"E127.bottom")])]});
            chamfer(context, id + "F78", {"entities" : qUnion([Q0, Q1, Q2, Q3, Q4, Q5, Q6, Q7]), "width" : 5 * mm, "tangentPropagation" : true});
        }
        {
            var Q0;
            Q0=makeQuery(id+"F43.opExtrude","CAP_EDGE",EDGE,{"disambiguationData":[OSD([sQuery(id+"F42.wireOp",EDGE,"E65.bottom")])],"isStart":false});
            var Q1;
            Q1=makeQuery(id+"F43.opExtrude","CAP_EDGE",EDGE,{"disambiguationData":[OSD([sQuery(id+"F42.wireOp",EDGE,"E65.top")])],"isStart":false});
            var Q2;
            Q2=makeQuery(id+"F43.opExtrude","CAP_EDGE",EDGE,{"disambiguationData":[OSD([sQuery(id+"F42.wireOp",EDGE,"E65.bottom")])],"isStart":true});
            var Q3;
            Q3=makeQuery(id+"F43.opExtrude","CAP_EDGE",EDGE,{"disambiguationData":[OSD([sQuery(id+"F42.wireOp",EDGE,"E65.top")])],"isStart":true});
            fillet(context, id + "F79", {"entities" : qUnion([Q0, Q1, Q2, Q3]), "radius" : 5 * mm, "tangentPropagation" : true, "allowEdgeOverflow" : false});
        }
        {
            var Q0;
            Q0=makeQuery(id+"F14.opExtrude","CAP_FACE",FACE,{"disambiguationData":[OSD([sQuery(id+"F1.wireOp",EDGE,"E0.top"),sQuery(id+"F3.wireOp",EDGE,"E3.bottom"),sQuery(id+"F3.wireOp",EDGE,"E3.right"),sQuery(id+"F3.wireOp",EDGE,"E4.bottom"),sQuery(id+"F3.wireOp",EDGE,"E4.right"),sQuery(id+"F13.wireOp",EDGE,"E10.bottom"),sQuery(id+"F13.wireOp",EDGE,"E10.top"),sQuery(id+"F13.wireOp",EDGE,"E10.left"),sQuery(id+"F13.wireOp",EDGE,"E10.right")])],"isStart":false});
            var sketch = newSketch(context, id + "F80", { "sketchPlane" : qUnion([Q0])});
            skLineSegment(sketch, "E148", {"start": v(50, 5) * mm, "end": v(50, 33) * mm, "construction": true});
            skPoint(sketch, "E148.endSnap0", {"position": v(50, 5) * mm});
            skLineSegment(sketch, "E149", {"start": v(-50, 5) * mm, "end": v(-50, 33) * mm, "construction": true});
            skCircle(sketch, "E150", {"center": v(50, 33) * mm, "radius": 2 * mm});
            skCircle(sketch, "E151", {"center": v(-50, 33) * mm, "radius": 2 * mm});
            skSolve(sketch);
        }
        {
            var Q0;
            Q0 = qSketchRegion(id + "F80", true);
            extrude(context, id + "F81", {"entities" : qUnion([Q0]), "operationType" : NewBodyOperationType.REMOVE, "oppositeDirection" : true, "depth" : 10 * mm});
        }
        {
            var Q0;
            {var subQ0=sQuery(id+"F19.wireOp",EDGE,"E15.top");var subQ2=sQuery(id+"F19.wireOp",EDGE,"E15.right");var subQ8=sQuery(id+"F19.wireOp",EDGE,"E15.left");var subQ9=sQuery(id+"F19.wireOp",EDGE,"E15.bottom");var subQ10=makeQuery(id+"F20.boolean.opBoolean","COPY",FACE,{"derivedFrom":makeQuery(id+"F20.opExtrude","CAP_FACE",FACE,{"disambiguationData":[OSD([subQ9,subQ0,subQ8,subQ2])],"isStart":false})});Q0=makeQuery(id+"F55.boolean.opBoolean","MERGE",FACE,{"derivedFrom":[makeQuery(id+"F53.boolean.opBoolean","SPLIT",FACE,{"disambiguationData":[TD([makeQuery(id+"F53.opExtrude","SWEPT_FACE",FACE,{"disambiguationData":[OSD([sQuery(id+"F52.wireOp",EDGE,"E75.bottom")])]})])],"derivedFrom":subQ10}),makeQuery(id+"F53.boolean.opBoolean","SPLIT",FACE,{"disambiguationData":[TD([makeQuery(id+"F53.opExtrude","SWEPT_FACE",FACE,{"disambiguationData":[OSD([sQuery(id+"F52.wireOp",EDGE,"E75.top")])]})])],"derivedFrom":subQ10}),makeQuery(id+"F53.boolean.opBoolean","SPLIT",FACE,{"disambiguationData":[TD([makeQuery(id+"F53.opExtrude","SWEPT_FACE",FACE,{"disambiguationData":[OSD([sQuery(id+"F52.wireOp",EDGE,"E76.left")])]})])],"derivedFrom":subQ10}),makeQuery(id+"F53.boolean.opBoolean","SPLIT",FACE,{"disambiguationData":[TD([makeQuery(id+"F53.opExtrude","SWEPT_FACE",FACE,{"disambiguationData":[OSD([sQuery(id+"F52.wireOp",EDGE,"E80")])]})])],"derivedFrom":subQ10}),makeQuery(id+"F55.opExtrude","CAP_FACE",FACE,{"disambiguationData":[OSD([sQuery(id+"F54.wireOp",EDGE,"E86.bottom"),sQuery(id+"F54.wireOp",EDGE,"E86.top"),sQuery(id+"F54.wireOp",EDGE,"E87.bottom"),sQuery(id+"F54.wireOp",EDGE,"E87.top"),sQuery(id+"F54.wireOp",EDGE,"E87.right"),sQuery(id+"F54.wireOp",EDGE,"E88.bottom"),sQuery(id+"F54.wireOp",EDGE,"E88.top"),sQuery(id+"F54.wireOp",EDGE,"E88.right")])],"isStart":false})]});}
            var sketch = newSketch(context, id + "F82", { "sketchPlane" : qUnion([Q0])});
            skCircle(sketch, "E152.0", {"center": v(-50, 33) * mm, "radius": 2 * mm});
            skCircle(sketch, "E153.0", {"center": v(50, 33) * mm, "radius": 2 * mm});
            skLineSegment(sketch, "E154.bottom", {"start": v(55, 28) * mm, "end": v(45, 28) * mm});
            skLineSegment(sketch, "E154.top", {"start": v(55, 38) * mm, "end": v(45, 38) * mm});
            skLineSegment(sketch, "E154.left", {"start": v(55, 28) * mm, "end": v(55, 38) * mm});
            skLineSegment(sketch, "E154.right", {"start": v(45, 28) * mm, "end": v(45, 38) * mm});
            skLineSegment(sketch, "E155.bottom", {"start": v(-55, 28) * mm, "end": v(-45, 28) * mm});
            skLineSegment(sketch, "E155.top", {"start": v(-55, 38) * mm, "end": v(-45, 38) * mm});
            skLineSegment(sketch, "E155.left", {"start": v(-55, 28) * mm, "end": v(-55, 38) * mm});
            skLineSegment(sketch, "E155.right", {"start": v(-45, 28) * mm, "end": v(-45, 38) * mm});
            skSolve(sketch);
        }
        {
            var Q0;
            Q0 = qSketchRegion(id + "F82", true);
            extrude(context, id + "F83", {"entities" : qUnion([Q0]), "operationType" : NewBodyOperationType.ADD, "depth" : 5 * mm});
        }
        {
            var Q0;
            Q0=makeQuery(id+"F14.opExtrude","CAP_FACE",FACE,{"disambiguationData":[OSD([sQuery(id+"F1.wireOp",EDGE,"E0.top"),sQuery(id+"F3.wireOp",EDGE,"E3.bottom"),sQuery(id+"F3.wireOp",EDGE,"E3.right"),sQuery(id+"F3.wireOp",EDGE,"E4.bottom"),sQuery(id+"F3.wireOp",EDGE,"E4.right"),sQuery(id+"F13.wireOp",EDGE,"E10.bottom"),sQuery(id+"F13.wireOp",EDGE,"E10.top"),sQuery(id+"F13.wireOp",EDGE,"E10.left"),sQuery(id+"F13.wireOp",EDGE,"E10.right")])],"isStart":false});
            var sketch = newSketch(context, id + "F84", { "sketchPlane" : qUnion([Q0])});
            skCircle(sketch, "E156", {"center": v(50, 33) * mm, "radius": 3.25 * mm});
            skCircle(sketch, "E157", {"center": v(-50, 33) * mm, "radius": 3.25 * mm});
            skSolve(sketch);
        }
        {
            var Q0;
            Q0 = qSketchRegion(id + "F84", true);
            extrude(context, id + "F85", {"entities" : qUnion([Q0]), "operationType" : NewBodyOperationType.REMOVE, "oppositeDirection" : true, "depth" : 5 * mm});
        }
        {
            var Q0;
            Q0=makeQuery(id+"F33.opExtrude","CAP_FACE",FACE,{"disambiguationData":[OSD([sQuery(id+"F32.wireOp",EDGE,"E43.0"),sQuery(id+"F32.wireOp",EDGE,"E44.top"),sQuery(id+"F32.wireOp",EDGE,"E44.left"),sQuery(id+"F32.wireOp",EDGE,"E44.right")])],"isStart":false});
            var sketch = newSketch(context, id + "F86", { "sketchPlane" : qUnion([Q0])});
            skLineSegment(sketch, "E158", {"start": v(-50, 5) * mm, "end": v(-50, 33) * mm, "construction": true});
            skLineSegment(sketch, "E159", {"start": v(50, 5) * mm, "end": v(50, 33) * mm, "construction": true});
            skCircle(sketch, "E160", {"center": v(-50, 33) * mm, "radius": 2 * mm});
            skCircle(sketch, "E161", {"center": v(50, 33) * mm, "radius": 2 * mm});
            skSolve(sketch);
        }
        {
            var Q0;
            Q0=makeQuery(id+"F33.opExtrude","CAP_FACE",FACE,{"disambiguationData":[OSD([sQuery(id+"F32.wireOp",EDGE,"E43.0"),sQuery(id+"F32.wireOp",EDGE,"E44.top"),sQuery(id+"F32.wireOp",EDGE,"E44.left"),sQuery(id+"F32.wireOp",EDGE,"E44.right")])],"isStart":false});
            var sketch = newSketch(context, id + "F87", { "sketchPlane" : qUnion([Q0])});
            skCircle(sketch, "E162", {"center": v(-50, 33) * mm, "radius": 3.25 * mm});
            skCircle(sketch, "E163", {"center": v(50, 33) * mm, "radius": 3.25 * mm});
            skSolve(sketch);
        }
        {
            var Q0;
            Q0 = qSketchRegion(id + "F87", true);
            extrude(context, id + "F88", {"entities" : qUnion([Q0]), "operationType" : NewBodyOperationType.REMOVE, "oppositeDirection" : true, "depth" : 5 * mm});
        }
        {
            var Q0;
            Q0=makeQuery(id+"F51.boolean.opBoolean","COPY",FACE,{"derivedFrom":makeQuery(id+"F51.opExtrude","CAP_FACE",FACE,{"disambiguationData":[OSD([sQuery(id+"F50.wireOp",EDGE,"E74.bottom"),sQuery(id+"F50.wireOp",EDGE,"E74.top"),sQuery(id+"F50.wireOp",EDGE,"E74.left"),sQuery(id+"F50.wireOp",EDGE,"E74.right")])],"isStart":false})});
            var sketch = newSketch(context, id + "F89", { "sketchPlane" : qUnion([Q0])});
            skLineSegment(sketch, "E164.bottom", {"start": v(55, 28) * mm, "end": v(45, 28) * mm});
            skLineSegment(sketch, "E164.top", {"start": v(55, 38) * mm, "end": v(45, 38) * mm});
            skLineSegment(sketch, "E164.left", {"start": v(55, 28) * mm, "end": v(55, 38) * mm});
            skLineSegment(sketch, "E164.right", {"start": v(45, 28) * mm, "end": v(45, 38) * mm});
            skPoint(sketch, "E164.middle", {"position": v(50, 33) * mm});
            skLineSegment(sketch, "E165.bottom", {"start": v(-55, 28) * mm, "end": v(-45, 28) * mm});
            skLineSegment(sketch, "E165.top", {"start": v(-55, 38) * mm, "end": v(-45, 38) * mm});
            skLineSegment(sketch, "E165.left", {"start": v(-55, 28) * mm, "end": v(-55, 38) * mm});
            skLineSegment(sketch, "E165.right", {"start": v(-45, 28) * mm, "end": v(-45, 38) * mm});
            skPoint(sketch, "E165.middle", {"position": v(-50, 33) * mm});
            skSolve(sketch);
        }
        {
            var Q0;
            Q0 = qSketchRegion(id + "F89", true);
            extrude(context, id + "F90", {"entities" : qUnion([Q0]), "operationType" : NewBodyOperationType.ADD, "depth" : 5 * mm});
        }
        {
            var Q0;
            Q0 = qSketchRegion(id + "F86", true);
            extrude(context, id + "F91", {"entities" : qUnion([Q0]), "operationType" : NewBodyOperationType.REMOVE, "oppositeDirection" : true, "depth" : 10 * mm, "hasDraft" : true, "draftAngle" : 3 * degree});
        }
        {
            var Q0;
            Q0=makeQuery(id+"F33.opExtrude","CAP_FACE",FACE,{"disambiguationData":[OSD([sQuery(id+"F32.wireOp",EDGE,"E43.0"),sQuery(id+"F32.wireOp",EDGE,"E44.top"),sQuery(id+"F32.wireOp",EDGE,"E44.left"),sQuery(id+"F32.wireOp",EDGE,"E44.right")])],"isStart":false});
            var sketch = newSketch(context, id + "F92", { "sketchPlane" : qUnion([Q0])});
            skLineSegment(sketch, "E166", {"start": v(-50, 5) * mm, "end": v(-50, 70) * mm, "construction": true});
            skLineSegment(sketch, "E167", {"start": v(50, 5) * mm, "end": v(50, 70) * mm, "construction": true});
            skCircle(sketch, "E168", {"center": v(50, 70) * mm, "radius": 2 * mm});
            skCircle(sketch, "E169", {"center": v(-50, 70) * mm, "radius": 2 * mm});
            skSolve(sketch);
        }
        {
            var Q0;
            Q0 = qSketchRegion(id + "F92", true);
            extrude(context, id + "F93", {"entities" : qUnion([Q0]), "operationType" : NewBodyOperationType.REMOVE, "oppositeDirection" : true, "depth" : 10 * mm});
        }
        {
            var Q0;
            Q0=makeQuery(id+"F33.opExtrude","CAP_FACE",FACE,{"disambiguationData":[OSD([sQuery(id+"F32.wireOp",EDGE,"E43.0"),sQuery(id+"F32.wireOp",EDGE,"E44.top"),sQuery(id+"F32.wireOp",EDGE,"E44.left"),sQuery(id+"F32.wireOp",EDGE,"E44.right")])],"isStart":false});
            var sketch = newSketch(context, id + "F94", { "sketchPlane" : qUnion([Q0])});
            skCircle(sketch, "E170", {"center": v(-50, 70) * mm, "radius": 3.25 * mm});
            skCircle(sketch, "E171", {"center": v(50, 70) * mm, "radius": 3.25 * mm});
            skSolve(sketch);
        }
        {
            var Q0;
            Q0 = qSketchRegion(id + "F94", true);
            extrude(context, id + "F95", {"entities" : qUnion([Q0]), "operationType" : NewBodyOperationType.REMOVE, "oppositeDirection" : true, "depth" : 5 * mm});
        }
        {
            var Q0;
            Q0 = qSketchRegion(id + "F92", true);
            extrude(context, id + "F96", {"entities" : qUnion([Q0]), "operationType" : NewBodyOperationType.REMOVE, "oppositeDirection" : true, "depth" : 10 * mm});
        }
        {
            var Q0;
            Q0=makeQuery(id+"F14.opExtrude","CAP_FACE",FACE,{"disambiguationData":[OSD([sQuery(id+"F1.wireOp",EDGE,"E0.top"),sQuery(id+"F3.wireOp",EDGE,"E3.bottom"),sQuery(id+"F3.wireOp",EDGE,"E3.right"),sQuery(id+"F3.wireOp",EDGE,"E4.bottom"),sQuery(id+"F3.wireOp",EDGE,"E4.right"),sQuery(id+"F13.wireOp",EDGE,"E10.bottom"),sQuery(id+"F13.wireOp",EDGE,"E10.top"),sQuery(id+"F13.wireOp",EDGE,"E10.left"),sQuery(id+"F13.wireOp",EDGE,"E10.right")])],"isStart":false});
            var sketch = newSketch(context, id + "F97", { "sketchPlane" : qUnion([Q0])});
            skLineSegment(sketch, "E172", {"start": v(50, 5) * mm, "end": v(50, 70) * mm, "construction": true});
            skLineSegment(sketch, "E173", {"start": v(-50, 5) * mm, "end": v(-50, 70) * mm, "construction": true});
            skCircle(sketch, "E174", {"center": v(50, 70) * mm, "radius": 3.25 * mm});
            skCircle(sketch, "E175", {"center": v(-50, 70) * mm, "radius": 3.25 * mm});
            skSolve(sketch);
        }
        {
            var Q0;
            Q0 = qSketchRegion(id + "F97", true);
            extrude(context, id + "F98", {"entities" : qUnion([Q0]), "operationType" : NewBodyOperationType.REMOVE, "oppositeDirection" : true, "depth" : 5 * mm});
        }
        {
            var Q0;
            {var subQ0=sQuery(id+"F19.wireOp",EDGE,"E15.top");var subQ2=sQuery(id+"F19.wireOp",EDGE,"E15.right");var subQ8=sQuery(id+"F19.wireOp",EDGE,"E15.left");var subQ9=sQuery(id+"F19.wireOp",EDGE,"E15.bottom");var subQ10=makeQuery(id+"F20.boolean.opBoolean","COPY",FACE,{"derivedFrom":makeQuery(id+"F20.opExtrude","CAP_FACE",FACE,{"disambiguationData":[OSD([subQ9,subQ0,subQ8,subQ2])],"isStart":false})});Q0=makeQuery(id+"F55.boolean.opBoolean","MERGE",FACE,{"derivedFrom":[makeQuery(id+"F53.boolean.opBoolean","SPLIT",FACE,{"disambiguationData":[TD([makeQuery(id+"F53.opExtrude","SWEPT_FACE",FACE,{"disambiguationData":[OSD([sQuery(id+"F52.wireOp",EDGE,"E75.bottom")])]})])],"derivedFrom":subQ10}),makeQuery(id+"F53.boolean.opBoolean","SPLIT",FACE,{"disambiguationData":[TD([makeQuery(id+"F53.opExtrude","SWEPT_FACE",FACE,{"disambiguationData":[OSD([sQuery(id+"F52.wireOp",EDGE,"E75.top")])]})])],"derivedFrom":subQ10}),makeQuery(id+"F53.boolean.opBoolean","SPLIT",FACE,{"disambiguationData":[TD([makeQuery(id+"F53.opExtrude","SWEPT_FACE",FACE,{"disambiguationData":[OSD([sQuery(id+"F52.wireOp",EDGE,"E76.left")])]})])],"derivedFrom":subQ10}),makeQuery(id+"F53.boolean.opBoolean","SPLIT",FACE,{"disambiguationData":[TD([makeQuery(id+"F53.opExtrude","SWEPT_FACE",FACE,{"disambiguationData":[OSD([sQuery(id+"F52.wireOp",EDGE,"E80")])]})])],"derivedFrom":subQ10}),makeQuery(id+"F55.opExtrude","CAP_FACE",FACE,{"disambiguationData":[OSD([sQuery(id+"F54.wireOp",EDGE,"E86.bottom"),sQuery(id+"F54.wireOp",EDGE,"E86.top"),sQuery(id+"F54.wireOp",EDGE,"E87.bottom"),sQuery(id+"F54.wireOp",EDGE,"E87.top"),sQuery(id+"F54.wireOp",EDGE,"E87.right"),sQuery(id+"F54.wireOp",EDGE,"E88.bottom"),sQuery(id+"F54.wireOp",EDGE,"E88.top"),sQuery(id+"F54.wireOp",EDGE,"E88.right")])],"isStart":false})]});}
            var sketch = newSketch(context, id + "F99", { "sketchPlane" : qUnion([Q0])});
            skLineSegment(sketch, "E176.bottom", {"start": v(-55, 65) * mm, "end": v(-45, 65) * mm});
            skLineSegment(sketch, "E176.top", {"start": v(-55, 75) * mm, "end": v(-45, 75) * mm});
            skLineSegment(sketch, "E176.left", {"start": v(-55, 65) * mm, "end": v(-55, 75) * mm});
            skLineSegment(sketch, "E176.right", {"start": v(-45, 65) * mm, "end": v(-45, 75) * mm});
            skPoint(sketch, "E176.middle", {"position": v(-50, 70) * mm});
            skLineSegment(sketch, "E177.bottom", {"start": v(55, 65) * mm, "end": v(45, 65) * mm});
            skLineSegment(sketch, "E177.top", {"start": v(55, 75) * mm, "end": v(45, 75) * mm});
            skLineSegment(sketch, "E177.left", {"start": v(55, 65) * mm, "end": v(55, 75) * mm});
            skLineSegment(sketch, "E177.right", {"start": v(45, 65) * mm, "end": v(45, 75) * mm});
            skPoint(sketch, "E177.middle", {"position": v(50, 70) * mm});
            skSolve(sketch);
        }
        {
            var Q0;
            Q0 = qSketchRegion(id + "F99", true);
            extrude(context, id + "F100", {"entities" : qUnion([Q0]), "operationType" : NewBodyOperationType.ADD, "depth" : 5 * mm});
        }
        {
            var Q0;
            Q0=makeQuery(id+"F14.opExtrude","CAP_FACE",FACE,{"disambiguationData":[OSD([sQuery(id+"F1.wireOp",EDGE,"E0.top"),sQuery(id+"F3.wireOp",EDGE,"E3.bottom"),sQuery(id+"F3.wireOp",EDGE,"E3.right"),sQuery(id+"F3.wireOp",EDGE,"E4.bottom"),sQuery(id+"F3.wireOp",EDGE,"E4.right"),sQuery(id+"F13.wireOp",EDGE,"E10.bottom"),sQuery(id+"F13.wireOp",EDGE,"E10.top"),sQuery(id+"F13.wireOp",EDGE,"E10.left"),sQuery(id+"F13.wireOp",EDGE,"E10.right")])],"isStart":false});
            var sketch = newSketch(context, id + "F101", { "sketchPlane" : qUnion([Q0])});
            skCircle(sketch, "E178", {"center": v(50, 70) * mm, "radius": 2 * mm});
            skCircle(sketch, "E179", {"center": v(-50, 70) * mm, "radius": 2 * mm});
            skSolve(sketch);
        }
        {
            var Q0;
            Q0 = qSketchRegion(id + "F101", true);
            extrude(context, id + "F102", {"entities" : qUnion([Q0]), "operationType" : NewBodyOperationType.REMOVE, "oppositeDirection" : true, "depth" : 10 * mm});
        }
        {
            var Q0;
            Q0=makeQuery(id+"F51.boolean.opBoolean","COPY",FACE,{"derivedFrom":makeQuery(id+"F51.opExtrude","CAP_FACE",FACE,{"disambiguationData":[OSD([sQuery(id+"F50.wireOp",EDGE,"E74.bottom"),sQuery(id+"F50.wireOp",EDGE,"E74.top"),sQuery(id+"F50.wireOp",EDGE,"E74.left"),sQuery(id+"F50.wireOp",EDGE,"E74.right")])],"isStart":false})});
            var sketch = newSketch(context, id + "F103", { "sketchPlane" : qUnion([Q0])});
            skLineSegment(sketch, "E180.bottom", {"start": v(55, 65) * mm, "end": v(45, 65) * mm});
            skLineSegment(sketch, "E180.top", {"start": v(55, 75) * mm, "end": v(45, 75) * mm});
            skLineSegment(sketch, "E180.left", {"start": v(55, 65) * mm, "end": v(55, 75) * mm});
            skLineSegment(sketch, "E180.right", {"start": v(45, 65) * mm, "end": v(45, 75) * mm});
            skPoint(sketch, "E180.middle", {"position": v(50, 70) * mm});
            skLineSegment(sketch, "E181.bottom", {"start": v(-55, 65) * mm, "end": v(-45, 65) * mm});
            skLineSegment(sketch, "E181.top", {"start": v(-55, 75) * mm, "end": v(-45, 75) * mm});
            skLineSegment(sketch, "E181.left", {"start": v(-55, 65) * mm, "end": v(-55, 75) * mm});
            skLineSegment(sketch, "E181.right", {"start": v(-45, 65) * mm, "end": v(-45, 75) * mm});
            skPoint(sketch, "E181.middle", {"position": v(-50, 70) * mm});
            skSolve(sketch);
        }
        {
            var Q0;
            Q0 = qSketchRegion(id + "F103", true);
            extrude(context, id + "F104", {"entities" : qUnion([Q0]), "operationType" : NewBodyOperationType.ADD, "depth" : 5 * mm});
        }
        {
            var Q0;
            Q0=makeQuery(id+"F33.opExtrude","CAP_FACE",FACE,{"disambiguationData":[OSD([sQuery(id+"F32.wireOp",EDGE,"E43.0"),sQuery(id+"F32.wireOp",EDGE,"E44.top"),sQuery(id+"F32.wireOp",EDGE,"E44.left"),sQuery(id+"F32.wireOp",EDGE,"E44.right")])],"isStart":false});
            var sketch = newSketch(context, id + "F105", { "sketchPlane" : qUnion([Q0])});
            skCircle(sketch, "E182", {"center": v(-50, 70) * mm, "radius": 2 * mm});
            skCircle(sketch, "E183", {"center": v(50, 70) * mm, "radius": 2 * mm});
            skSolve(sketch);
        }
        {
            var Q0;
            Q0 = qSketchRegion(id + "F105", true);
            extrude(context, id + "F106", {"entities" : qUnion([Q0]), "operationType" : NewBodyOperationType.REMOVE, "oppositeDirection" : true, "depth" : 10 * mm});
        }
        {
            var Q0;
            Q0=makeQuery(id+"F33.opExtrude","CAP_FACE",FACE,{"disambiguationData":[OSD([sQuery(id+"F32.wireOp",EDGE,"E43.0"),sQuery(id+"F32.wireOp",EDGE,"E44.top"),sQuery(id+"F32.wireOp",EDGE,"E44.left"),sQuery(id+"F32.wireOp",EDGE,"E44.right")])],"isStart":false});
            var sketch = newSketch(context, id + "F107", { "sketchPlane" : qUnion([Q0])});
            skLineSegment(sketch, "E184.bottom", {"start": v(-45, 95) * mm, "end": v(45, 95) * mm});
            skLineSegment(sketch, "E184.top", {"start": v(-45, 35) * mm, "end": v(45, 35) * mm});
            skLineSegment(sketch, "E184.left", {"start": v(-45, 95) * mm, "end": v(-45, 35) * mm});
            skLineSegment(sketch, "E184.right", {"start": v(45, 95) * mm, "end": v(45, 35) * mm});
            skSolve(sketch);
        }
        {
            var Q0;
            Q0 = qSketchRegion(id + "F107", true);
            extrude(context, id + "F108", {"entities" : qUnion([Q0]), "operationType" : NewBodyOperationType.REMOVE, "oppositeDirection" : true, "depth" : 5 * mm});
        }
        {
            var Q0;
            Q0=makeQuery(id+"F71.opExtrude","CAP_FACE",FACE,{"disambiguationData":[OSD([sQuery(id+"F70.wireOp",EDGE,"E119"),sQuery(id+"F70.wireOp",EDGE,"E120.bottom"),sQuery(id+"F70.wireOp",EDGE,"E120.top"),sQuery(id+"F70.wireOp",EDGE,"E120.left"),sQuery(id+"F70.wireOp",EDGE,"E120.right"),sQuery(id+"F70.wireOp",EDGE,"E121.bottom"),sQuery(id+"F70.wireOp",EDGE,"E121.top"),sQuery(id+"F70.wireOp",EDGE,"E121.left"),sQuery(id+"F70.wireOp",EDGE,"E121.right"),sQuery(id+"F70.wireOp",EDGE,"E122.bottom"),sQuery(id+"F70.wireOp",EDGE,"E122.top"),sQuery(id+"F70.wireOp",EDGE,"E122.left"),sQuery(id+"F70.wireOp",EDGE,"E122.right"),sQuery(id+"F70.wireOp",EDGE,"E123.bottom"),sQuery(id+"F70.wireOp",EDGE,"E123.top"),sQuery(id+"F70.wireOp",EDGE,"E123.left"),sQuery(id+"F70.wireOp",EDGE,"E123.right"),sQuery(id+"F70.wireOp",EDGE,"E124.left"),sQuery(id+"F70.wireOp",EDGE,"E124.right"),sQuery(id+"F70.wireOp",EDGE,"E125.left"),sQuery(id+"F70.wireOp",EDGE,"E125.right"),sQuery(id+"F70.wireOp",EDGE,"E126.bottom"),sQuery(id+"F70.wireOp",EDGE,"E126.top"),sQuery(id+"F70.wireOp",EDGE,"E127.bottom"),sQuery(id+"F70.wireOp",EDGE,"E127.top"),sQuery(id+"F70.wireOp",EDGE,"E128"),sQuery(id+"F70.wireOp",EDGE,"E129"),sQuery(id+"F70.wireOp",EDGE,"E130")])],"isStart":true});
            var sketch = newSketch(context, id + "F109", { "sketchPlane" : qUnion([Q0])});
            skLineSegment(sketch, "E185", {"start": v(33.33, 2.23) * mm, "end": v(28.33, 2.23) * mm, "construction": true});
            skLineSegment(sketch, "E186.bottom", {"start": v(28.33, -7.77) * mm, "end": v(33.33, -7.77) * mm});
            skLineSegment(sketch, "E186.top", {"start": v(28.33, 12.23) * mm, "end": v(33.33, 12.23) * mm});
            skLineSegment(sketch, "E186.left", {"start": v(28.33, -7.77) * mm, "end": v(28.33, 12.23) * mm});
            skLineSegment(sketch, "E186.right", {"start": v(33.33, -7.77) * mm, "end": v(33.33, 12.23) * mm});
            skPoint(sketch, "E186.middle", {"position": v(30.83, 2.23) * mm});
            skSolve(sketch);
        }
        {
            var Q0;
            Q0 = qSketchRegion(id + "F109", true);
            extrude(context, id + "F110", {"entities" : qUnion([Q0]), "operationType" : NewBodyOperationType.ADD, "depth" : 6 * mm});
        }
        {
            var Q0;
            Q0=makeQuery(id+"F14.opExtrude","CAP_FACE",FACE,{"disambiguationData":[OSD([sQuery(id+"F1.wireOp",EDGE,"E0.top"),sQuery(id+"F3.wireOp",EDGE,"E3.bottom"),sQuery(id+"F3.wireOp",EDGE,"E3.right"),sQuery(id+"F3.wireOp",EDGE,"E4.bottom"),sQuery(id+"F3.wireOp",EDGE,"E4.right"),sQuery(id+"F13.wireOp",EDGE,"E10.bottom"),sQuery(id+"F13.wireOp",EDGE,"E10.top"),sQuery(id+"F13.wireOp",EDGE,"E10.left"),sQuery(id+"F13.wireOp",EDGE,"E10.right")])],"isStart":false});
            var sketch = newSketch(context, id + "F111", { "sketchPlane" : qUnion([Q0])});
            skText(sketch, "E187", { "text": "smartCube", "fontName": "RobotoSlab-Regular.ttf"});
            const initialGuessF111  = {"E187": [-0.03587, 0.02507, 1, 0, 0.01]};
            skSetInitialGuess(sketch, initialGuessF111);
            skSolve(sketch);
        }
        {
            var Q0;
            Q0 = qSketchRegion(id + "F111", true);
            extrude(context, id + "F112", {"entities" : qUnion([Q0]), "operationType" : NewBodyOperationType.REMOVE, "oppositeDirection" : true, "depth" : 10 * mm});
        }
        {
            var Q0;
            {var subQ3=sQuery(id+"F32.wireOp",EDGE,"E44.left");var subQ4=makeQuery(id+"F33.opExtrude","SWEPT_FACE",FACE,{"disambiguationData":[OSD([subQ3])]});var subQ9=sQuery(id+"F50.wireOp",EDGE,"E74.top");var subQ10=sQuery(id+"F50.wireOp",EDGE,"E74.bottom");var subQ11=makeQuery(id+"F51.opExtrude","CAP_FACE",FACE,{"disambiguationData":[OSD([subQ10,subQ9,sQuery(id+"F50.wireOp",EDGE,"E74.left"),sQuery(id+"F50.wireOp",EDGE,"E74.right")])],"isStart":false});var subQ12=makeQuery(id+"F35.boolean.opBoolean","COPY",FACE,{"derivedFrom":makeQuery(id+"F35.opExtrude","SWEPT_FACE",FACE,{"disambiguationData":[OSD([sQuery(id+"F34.wireOp",EDGE,"E50.bottom")])]})});Q0=makeQuery(id+"F108.boolean.opBoolean","SPLIT",FACE,{"disambiguationData":[TD([subQ12])],"derivedFrom":makeQuery(id+"F90.boolean.opBoolean","SPLIT",FACE,{"disambiguationData":[TD([subQ4])],"derivedFrom":makeQuery(id+"F51.boolean.opBoolean","COPY",FACE,{"derivedFrom":subQ11})})});}
            var sketch = newSketch(context, id + "F113", { "sketchPlane" : qUnion([Q0])});
            skCircle(sketch, "E188", {"center": v(24.89, 19.89) * mm, "radius": 1.75 * mm});
            skCircle(sketch, "E189", {"center": v(45.89, 19.89) * mm, "radius": 1.75 * mm});
            skLineSegment(sketch, "E190", {"start": v(24.89, 19.89) * mm, "end": v(45.89, 19.89) * mm, "construction": true});
            skLineSegment(sketch, "E191.bottom", {"start": v(48.39, 14.39) * mm, "end": v(22.39, 14.39) * mm});
            skLineSegment(sketch, "E191.top", {"start": v(48.39, 25.39) * mm, "end": v(22.39, 25.39) * mm});
            skLineSegment(sketch, "E191.left", {"start": v(48.39, 14.39) * mm, "end": v(48.39, 25.39) * mm});
            skLineSegment(sketch, "E191.right", {"start": v(22.39, 14.39) * mm, "end": v(22.39, 25.39) * mm});
            skPoint(sketch, "E191.middle", {"position": v(35.39, 19.89) * mm});
            skLineSegment(sketch, "E192.bottom", {"start": v(40.39, 17.39) * mm, "end": v(30.39, 17.39) * mm});
            skLineSegment(sketch, "E192.top", {"start": v(40.39, 22.39) * mm, "end": v(30.39, 22.39) * mm});
            skLineSegment(sketch, "E192.left", {"start": v(40.39, 17.39) * mm, "end": v(40.39, 22.39) * mm});
            skLineSegment(sketch, "E192.right", {"start": v(30.39, 17.39) * mm, "end": v(30.39, 22.39) * mm});
            skSolve(sketch);
        }
        {
            var Q0;
            Q0=makeQuery(id+"F113.imprint","IMPRINT",FACE,{"disambiguationData":[TD([[makeQuery(id+"F113.imprint","IMPRINT",EDGE,{"derivedFrom":sQuery(id+"F113.wireOp",EDGE,"E192.bottom")}),-1.0]])]});
            var Q1;
            Q1=makeQuery(id+"F113.imprint","IMPRINT",FACE,{"disambiguationData":[TD([[makeQuery(id+"F113.imprint","IMPRINT",EDGE,{"derivedFrom":sQuery(id+"F113.wireOp",EDGE,"E188")}),1.0]])]});
            var Q2;
            Q2=makeQuery(id+"F113.imprint","IMPRINT",FACE,{"disambiguationData":[TD([[makeQuery(id+"F113.imprint","IMPRINT",EDGE,{"derivedFrom":sQuery(id+"F113.wireOp",EDGE,"E189")}),1.0]])]});
            extrude(context, id + "F114", {"entities" : qUnion([Q0, Q1, Q2]), "operationType" : NewBodyOperationType.REMOVE, "oppositeDirection" : true, "depth" : 5 * mm});
        }
        {
            var Q0;
            Q0=makeQuery(id+"F113.imprint","IMPRINT",FACE,{"disambiguationData":[TD([[makeQuery(id+"F113.imprint","IMPRINT",EDGE,{"derivedFrom":sQuery(id+"F113.wireOp",EDGE,"E188")}),-1.0]])]});
            extrude(context, id + "F115", {"entities" : qUnion([Q0]), "operationType" : NewBodyOperationType.REMOVE, "oppositeDirection" : true, "depth" : 3 * mm});
        }
        {
            var Q0;
            Q0=makeQuery(id+"F43.opExtrude","CAP_FACE",FACE,{"disambiguationData":[OSD([sQuery(id+"F42.wireOp",EDGE,"E65.bottom"),sQuery(id+"F42.wireOp",EDGE,"E65.top"),sQuery(id+"F42.wireOp",EDGE,"E65.left"),sQuery(id+"F42.wireOp",EDGE,"E65.right")])],"isStart":true});
            var sketch = newSketch(context, id + "F116", { "sketchPlane" : qUnion([Q0])});
            skCircle(sketch, "E193", {"center": v(39, -9.8) * mm, "radius": 1.5 * mm});
            skCircle(sketch, "E194", {"center": v(-35, -9.8) * mm, "radius": 1.5 * mm});
            skLineSegment(sketch, "E195", {"start": v(-35, -9.8) * mm, "end": v(39, -9.8) * mm, "construction": true});
            skLineSegment(sketch, "E196.bottom", {"start": v(-55, -44.8) * mm, "end": v(-44.8, -44.8) * mm, "construction": true});
            skLineSegment(sketch, "E196.top", {"start": v(-55, -34.6) * mm, "end": v(-44.8, -34.6) * mm, "construction": true});
            skLineSegment(sketch, "E196.left", {"start": v(-55, -44.8) * mm, "end": v(-55, -34.6) * mm, "construction": true});
            skLineSegment(sketch, "E196.right", {"start": v(-44.8, -44.8) * mm, "end": v(-44.8, -34.6) * mm, "construction": true});
            skLineSegment(sketch, "E197.bottom", {"start": v(55, -44.8) * mm, "end": v(44.8, -44.8) * mm, "construction": true});
            skLineSegment(sketch, "E197.top", {"start": v(55, -34.6) * mm, "end": v(44.8, -34.6) * mm, "construction": true});
            skLineSegment(sketch, "E197.left", {"start": v(55, -44.8) * mm, "end": v(55, -34.6) * mm, "construction": true});
            skLineSegment(sketch, "E197.right", {"start": v(44.8, -44.8) * mm, "end": v(44.8, -34.6) * mm, "construction": true});
            skPoint(sketch, "E198.firstSnap0", {"position": v(-49.9, -34.6) * mm});
            skPoint(sketch, "E198.firstSnap1", {"position": v(-44.8, -39.7) * mm});
            skPoint(sketch, "E198.oppositeSnap0", {"position": v(49.9, -34.6) * mm});
            skLineSegment(sketch, "E198.bottom", {"start": v(-49.9, -39.7) * mm, "end": v(49.9, -39.7) * mm});
            skLineSegment(sketch, "E198.top", {"start": v(-49.9, -19.7) * mm, "end": v(49.9, -19.7) * mm});
            skLineSegment(sketch, "E198.left", {"start": v(-49.9, -39.7) * mm, "end": v(-49.9, -19.7) * mm});
            skLineSegment(sketch, "E198.right", {"start": v(49.9, -39.7) * mm, "end": v(49.9, -19.7) * mm});
            skLineSegment(sketch, "E199.bottom", {"start": v(-44.8, 44.8) * mm, "end": v(-55, 44.8) * mm, "construction": true});
            skLineSegment(sketch, "E199.top", {"start": v(-44.8, 34.6) * mm, "end": v(-55, 34.6) * mm, "construction": true});
            skLineSegment(sketch, "E199.left", {"start": v(-44.8, 44.8) * mm, "end": v(-44.8, 34.6) * mm, "construction": true});
            skLineSegment(sketch, "E199.right", {"start": v(-55, 44.8) * mm, "end": v(-55, 34.6) * mm, "construction": true});
            skLineSegment(sketch, "E200.bottom", {"start": v(44.8, 44.8) * mm, "end": v(55, 44.8) * mm, "construction": true});
            skLineSegment(sketch, "E200.top", {"start": v(44.8, 34.6) * mm, "end": v(55, 34.6) * mm, "construction": true});
            skLineSegment(sketch, "E200.left", {"start": v(44.8, 44.8) * mm, "end": v(44.8, 34.6) * mm, "construction": true});
            skLineSegment(sketch, "E200.right", {"start": v(55, 44.8) * mm, "end": v(55, 34.6) * mm, "construction": true});
            skPoint(sketch, "E201.firstSnap0", {"position": v(-44.8, 39.7) * mm});
            skPoint(sketch, "E201.firstSnap1", {"position": v(-49.9, 34.6) * mm});
            skPoint(sketch, "E201.oppositeSnap0", {"position": v(49.9, 34.6) * mm});
            skLineSegment(sketch, "E201.bottom", {"start": v(-49.9, 39.7) * mm, "end": v(49.9, 39.7) * mm});
            skLineSegment(sketch, "E201.top", {"start": v(-49.9, -0.3) * mm, "end": v(49.9, -0.3) * mm});
            skLineSegment(sketch, "E201.left", {"start": v(-49.9, 39.7) * mm, "end": v(-49.9, -0.3) * mm});
            skLineSegment(sketch, "E201.right", {"start": v(49.9, 39.7) * mm, "end": v(49.9, -0.3) * mm});
            skLineSegment(sketch, "E202.bottom", {"start": v(32, -16.3) * mm, "end": v(-28, -16.3) * mm});
            skLineSegment(sketch, "E202.top", {"start": v(32, -3.3) * mm, "end": v(-28, -3.3) * mm});
            skLineSegment(sketch, "E202.left", {"start": v(32, -16.3) * mm, "end": v(32, -3.3) * mm});
            skLineSegment(sketch, "E202.right", {"start": v(-28, -16.3) * mm, "end": v(-28, -3.3) * mm});
            skPoint(sketch, "E202.middle", {"position": v(2, -9.8) * mm});
            skSolve(sketch);
        }
        {
            var Q0;
            Q0=makeQuery(id+"F116.imprint","IMPRINT",FACE,{"disambiguationData":[TD([[makeQuery(id+"F116.imprint","IMPRINT",EDGE,{"derivedFrom":sQuery(id+"F116.wireOp",EDGE,"E201.bottom")}),-1.0]])]});
            var Q1;
            Q1=makeQuery(id+"F116.imprint","IMPRINT",FACE,{"disambiguationData":[TD([[makeQuery(id+"F116.imprint","IMPRINT",EDGE,{"derivedFrom":sQuery(id+"F116.wireOp",EDGE,"E198.bottom")}),1.0]])]});
            var Q2;
            Q2=makeQuery(id+"F116.imprint","IMPRINT",FACE,{"disambiguationData":[TD([[makeQuery(id+"F116.imprint","IMPRINT",EDGE,{"derivedFrom":sQuery(id+"F116.wireOp",EDGE,"E194")}),1.0]])]});
            var Q3;
            Q3=makeQuery(id+"F116.imprint","IMPRINT",FACE,{"disambiguationData":[TD([[makeQuery(id+"F116.imprint","IMPRINT",EDGE,{"derivedFrom":sQuery(id+"F116.wireOp",EDGE,"E193")}),1.0]])]});
            var Q4;
            Q4=makeQuery(id+"F116.imprint","IMPRINT",FACE,{"disambiguationData":[TD([[makeQuery(id+"F116.imprint","IMPRINT",EDGE,{"derivedFrom":sQuery(id+"F116.wireOp",EDGE,"E202.bottom")}),-1.0]])]});
            extrude(context, id + "F117", {"entities" : qUnion([Q0, Q1, Q2, Q3, Q4]), "operationType" : NewBodyOperationType.REMOVE, "oppositeDirection" : true, "depth" : 5 * mm});
        }
        {
            var Q0;
            Q0=makeQuery(id+"F71.opExtrude","CAP_FACE",FACE,{"disambiguationData":[OSD([sQuery(id+"F70.wireOp",EDGE,"E119"),sQuery(id+"F70.wireOp",EDGE,"E120.bottom"),sQuery(id+"F70.wireOp",EDGE,"E120.top"),sQuery(id+"F70.wireOp",EDGE,"E120.left"),sQuery(id+"F70.wireOp",EDGE,"E120.right"),sQuery(id+"F70.wireOp",EDGE,"E121.bottom"),sQuery(id+"F70.wireOp",EDGE,"E121.top"),sQuery(id+"F70.wireOp",EDGE,"E121.left"),sQuery(id+"F70.wireOp",EDGE,"E121.right"),sQuery(id+"F70.wireOp",EDGE,"E122.bottom"),sQuery(id+"F70.wireOp",EDGE,"E122.top"),sQuery(id+"F70.wireOp",EDGE,"E122.left"),sQuery(id+"F70.wireOp",EDGE,"E122.right"),sQuery(id+"F70.wireOp",EDGE,"E123.bottom"),sQuery(id+"F70.wireOp",EDGE,"E123.top"),sQuery(id+"F70.wireOp",EDGE,"E123.left"),sQuery(id+"F70.wireOp",EDGE,"E123.right"),sQuery(id+"F70.wireOp",EDGE,"E124.left"),sQuery(id+"F70.wireOp",EDGE,"E124.right"),sQuery(id+"F70.wireOp",EDGE,"E125.left"),sQuery(id+"F70.wireOp",EDGE,"E125.right"),sQuery(id+"F70.wireOp",EDGE,"E126.bottom"),sQuery(id+"F70.wireOp",EDGE,"E126.top"),sQuery(id+"F70.wireOp",EDGE,"E127.bottom"),sQuery(id+"F70.wireOp",EDGE,"E127.top"),sQuery(id+"F70.wireOp",EDGE,"E128"),sQuery(id+"F70.wireOp",EDGE,"E129"),sQuery(id+"F70.wireOp",EDGE,"E130"),sQuery(id+"F70.wireOp",EDGE,"E131.top")])],"isStart":false});
            var sketch = newSketch(context, id + "F118", { "sketchPlane" : qUnion([Q0])});
            skLineSegment(sketch, "E203.bottom", {"start": v(56.33, -37.23) * mm, "end": v(38.33, -37.23) * mm});
            skLineSegment(sketch, "E203.top", {"start": v(56.33, -40.23) * mm, "end": v(38.33, -40.23) * mm});
            skLineSegment(sketch, "E203.left", {"start": v(56.33, -37.23) * mm, "end": v(56.33, -40.23) * mm});
            skLineSegment(sketch, "E203.right", {"start": v(38.33, -37.23) * mm, "end": v(38.33, -40.23) * mm});
            skLineSegment(sketch, "E204.bottom", {"start": v(23.33, -37.23) * mm, "end": v(-20.67, -37.23) * mm});
            skLineSegment(sketch, "E204.top", {"start": v(23.33, -40.23) * mm, "end": v(-20.67, -40.23) * mm});
            skLineSegment(sketch, "E204.left", {"start": v(23.33, -37.23) * mm, "end": v(23.33, -40.23) * mm});
            skLineSegment(sketch, "E204.right", {"start": v(-20.67, -37.23) * mm, "end": v(-20.67, -40.23) * mm});
            skLineSegment(sketch, "E205.bottom", {"start": v(-35.67, -37.23) * mm, "end": v(-53.67, -37.23) * mm});
            skLineSegment(sketch, "E205.top", {"start": v(-35.67, -40.23) * mm, "end": v(-53.67, -40.23) * mm});
            skLineSegment(sketch, "E205.left", {"start": v(-35.67, -37.23) * mm, "end": v(-35.67, -40.23) * mm});
            skLineSegment(sketch, "E205.right", {"start": v(-53.67, -37.23) * mm, "end": v(-53.67, -40.23) * mm});
            skLineSegment(sketch, "E206.bottom", {"start": v(38.33, 32.77) * mm, "end": v(56.33, 32.77) * mm});
            skLineSegment(sketch, "E206.top", {"start": v(38.33, 35.77) * mm, "end": v(56.33, 35.77) * mm});
            skLineSegment(sketch, "E206.left", {"start": v(38.33, 32.77) * mm, "end": v(38.33, 35.77) * mm});
            skLineSegment(sketch, "E206.right", {"start": v(56.33, 32.77) * mm, "end": v(56.33, 35.77) * mm});
            skLineSegment(sketch, "E207.bottom", {"start": v(23.33, 32.77) * mm, "end": v(-20.67, 32.77) * mm});
            skLineSegment(sketch, "E207.top", {"start": v(23.33, 35.77) * mm, "end": v(-20.67, 35.77) * mm});
            skLineSegment(sketch, "E207.left", {"start": v(23.33, 32.77) * mm, "end": v(23.33, 35.77) * mm});
            skLineSegment(sketch, "E207.right", {"start": v(-20.67, 32.77) * mm, "end": v(-20.67, 35.77) * mm});
            skLineSegment(sketch, "E208.bottom", {"start": v(-35.67, 32.77) * mm, "end": v(-53.67, 32.77) * mm});
            skLineSegment(sketch, "E208.top", {"start": v(-35.67, 35.77) * mm, "end": v(-53.67, 35.77) * mm});
            skLineSegment(sketch, "E208.left", {"start": v(-35.67, 32.77) * mm, "end": v(-35.67, 35.77) * mm});
            skLineSegment(sketch, "E208.right", {"start": v(-53.67, 32.77) * mm, "end": v(-53.67, 35.77) * mm});
            skSolve(sketch);
        }
        {
            var Q0;
            Q0 = qSketchRegion(id + "F118", true);
            extrude(context, id + "F119", {"entities" : qUnion([Q0]), "operationType" : NewBodyOperationType.REMOVE, "oppositeDirection" : true, "depth" : 10 * mm});
        }
        {
            var Q0;
            Q0=makeQuery(id+"F71.opExtrude","CAP_FACE",FACE,{"disambiguationData":[OSD([sQuery(id+"F70.wireOp",EDGE,"E119"),sQuery(id+"F70.wireOp",EDGE,"E120.bottom"),sQuery(id+"F70.wireOp",EDGE,"E120.top"),sQuery(id+"F70.wireOp",EDGE,"E120.left"),sQuery(id+"F70.wireOp",EDGE,"E120.right"),sQuery(id+"F70.wireOp",EDGE,"E121.bottom"),sQuery(id+"F70.wireOp",EDGE,"E121.top"),sQuery(id+"F70.wireOp",EDGE,"E121.left"),sQuery(id+"F70.wireOp",EDGE,"E121.right"),sQuery(id+"F70.wireOp",EDGE,"E122.bottom"),sQuery(id+"F70.wireOp",EDGE,"E122.top"),sQuery(id+"F70.wireOp",EDGE,"E122.left"),sQuery(id+"F70.wireOp",EDGE,"E122.right"),sQuery(id+"F70.wireOp",EDGE,"E123.bottom"),sQuery(id+"F70.wireOp",EDGE,"E123.top"),sQuery(id+"F70.wireOp",EDGE,"E123.left"),sQuery(id+"F70.wireOp",EDGE,"E123.right"),sQuery(id+"F70.wireOp",EDGE,"E124.left"),sQuery(id+"F70.wireOp",EDGE,"E124.right"),sQuery(id+"F70.wireOp",EDGE,"E125.left"),sQuery(id+"F70.wireOp",EDGE,"E125.right"),sQuery(id+"F70.wireOp",EDGE,"E126.bottom"),sQuery(id+"F70.wireOp",EDGE,"E126.top"),sQuery(id+"F70.wireOp",EDGE,"E127.bottom"),sQuery(id+"F70.wireOp",EDGE,"E127.top"),sQuery(id+"F70.wireOp",EDGE,"E128"),sQuery(id+"F70.wireOp",EDGE,"E129"),sQuery(id+"F70.wireOp",EDGE,"E130"),sQuery(id+"F70.wireOp",EDGE,"E131.top")])],"isStart":false});
            var sketch = newSketch(context, id + "F120", { "sketchPlane" : qUnion([Q0])});
            skLineSegment(sketch, "E209.bottom", {"start": v(23.33, -40.23) * mm, "end": v(25.83, -40.23) * mm});
            skLineSegment(sketch, "E209.top", {"start": v(23.33, -34.73) * mm, "end": v(25.83, -34.73) * mm});
            skLineSegment(sketch, "E209.left", {"start": v(23.33, -40.23) * mm, "end": v(23.33, -34.73) * mm});
            skLineSegment(sketch, "E209.right", {"start": v(25.83, -40.23) * mm, "end": v(25.83, -34.73) * mm});
            skLineSegment(sketch, "E210.bottom", {"start": v(38.33, -40.23) * mm, "end": v(35.83, -40.23) * mm});
            skLineSegment(sketch, "E210.top", {"start": v(38.33, -34.73) * mm, "end": v(35.83, -34.73) * mm});
            skLineSegment(sketch, "E210.left", {"start": v(38.33, -40.23) * mm, "end": v(38.33, -34.73) * mm});
            skLineSegment(sketch, "E210.right", {"start": v(35.83, -40.23) * mm, "end": v(35.83, -34.73) * mm});
            skLineSegment(sketch, "E211.bottom", {"start": v(38.33, 35.77) * mm, "end": v(35.83, 35.77) * mm});
            skLineSegment(sketch, "E211.top", {"start": v(38.33, 30.27) * mm, "end": v(35.83, 30.27) * mm});
            skLineSegment(sketch, "E211.left", {"start": v(38.33, 35.77) * mm, "end": v(38.33, 30.27) * mm});
            skLineSegment(sketch, "E211.right", {"start": v(35.83, 35.77) * mm, "end": v(35.83, 30.27) * mm});
            skLineSegment(sketch, "E212.bottom", {"start": v(23.33, 35.77) * mm, "end": v(25.83, 35.77) * mm});
            skLineSegment(sketch, "E212.top", {"start": v(23.33, 30.27) * mm, "end": v(25.83, 30.27) * mm});
            skLineSegment(sketch, "E212.left", {"start": v(23.33, 35.77) * mm, "end": v(23.33, 30.27) * mm});
            skLineSegment(sketch, "E212.right", {"start": v(25.83, 35.77) * mm, "end": v(25.83, 30.27) * mm});
            skLineSegment(sketch, "E213.bottom", {"start": v(-20.67, 35.77) * mm, "end": v(-23.17, 35.77) * mm});
            skLineSegment(sketch, "E213.top", {"start": v(-20.67, 30.27) * mm, "end": v(-23.17, 30.27) * mm});
            skLineSegment(sketch, "E213.left", {"start": v(-20.67, 35.77) * mm, "end": v(-20.67, 30.27) * mm});
            skLineSegment(sketch, "E213.right", {"start": v(-23.17, 35.77) * mm, "end": v(-23.17, 30.27) * mm});
            skLineSegment(sketch, "E214.bottom", {"start": v(-35.67, 35.77) * mm, "end": v(-33.17, 35.77) * mm});
            skLineSegment(sketch, "E214.top", {"start": v(-35.67, 30.27) * mm, "end": v(-33.17, 30.27) * mm});
            skLineSegment(sketch, "E214.left", {"start": v(-35.67, 35.77) * mm, "end": v(-35.67, 30.27) * mm});
            skLineSegment(sketch, "E214.right", {"start": v(-33.17, 35.77) * mm, "end": v(-33.17, 30.27) * mm});
            skLineSegment(sketch, "E215.bottom", {"start": v(-35.67, -40.23) * mm, "end": v(-33.17, -40.23) * mm});
            skLineSegment(sketch, "E215.top", {"start": v(-35.67, -34.73) * mm, "end": v(-33.17, -34.73) * mm});
            skLineSegment(sketch, "E215.left", {"start": v(-35.67, -40.23) * mm, "end": v(-35.67, -34.73) * mm});
            skLineSegment(sketch, "E215.right", {"start": v(-33.17, -40.23) * mm, "end": v(-33.17, -34.73) * mm});
            skLineSegment(sketch, "E216.bottom", {"start": v(-20.67, -40.23) * mm, "end": v(-23.17, -40.23) * mm});
            skLineSegment(sketch, "E216.top", {"start": v(-20.67, -34.73) * mm, "end": v(-23.17, -34.73) * mm});
            skLineSegment(sketch, "E216.left", {"start": v(-20.67, -40.23) * mm, "end": v(-20.67, -34.73) * mm});
            skLineSegment(sketch, "E216.right", {"start": v(-23.17, -40.23) * mm, "end": v(-23.17, -34.73) * mm});
            skSolve(sketch);
        }
        {
            var Q0;
            Q0 = qSketchRegion(id + "F120", true);
            extrude(context, id + "F121", {"entities" : qUnion([Q0]), "operationType" : NewBodyOperationType.REMOVE, "oppositeDirection" : true, "depth" : 5 * mm});
        }
    });
